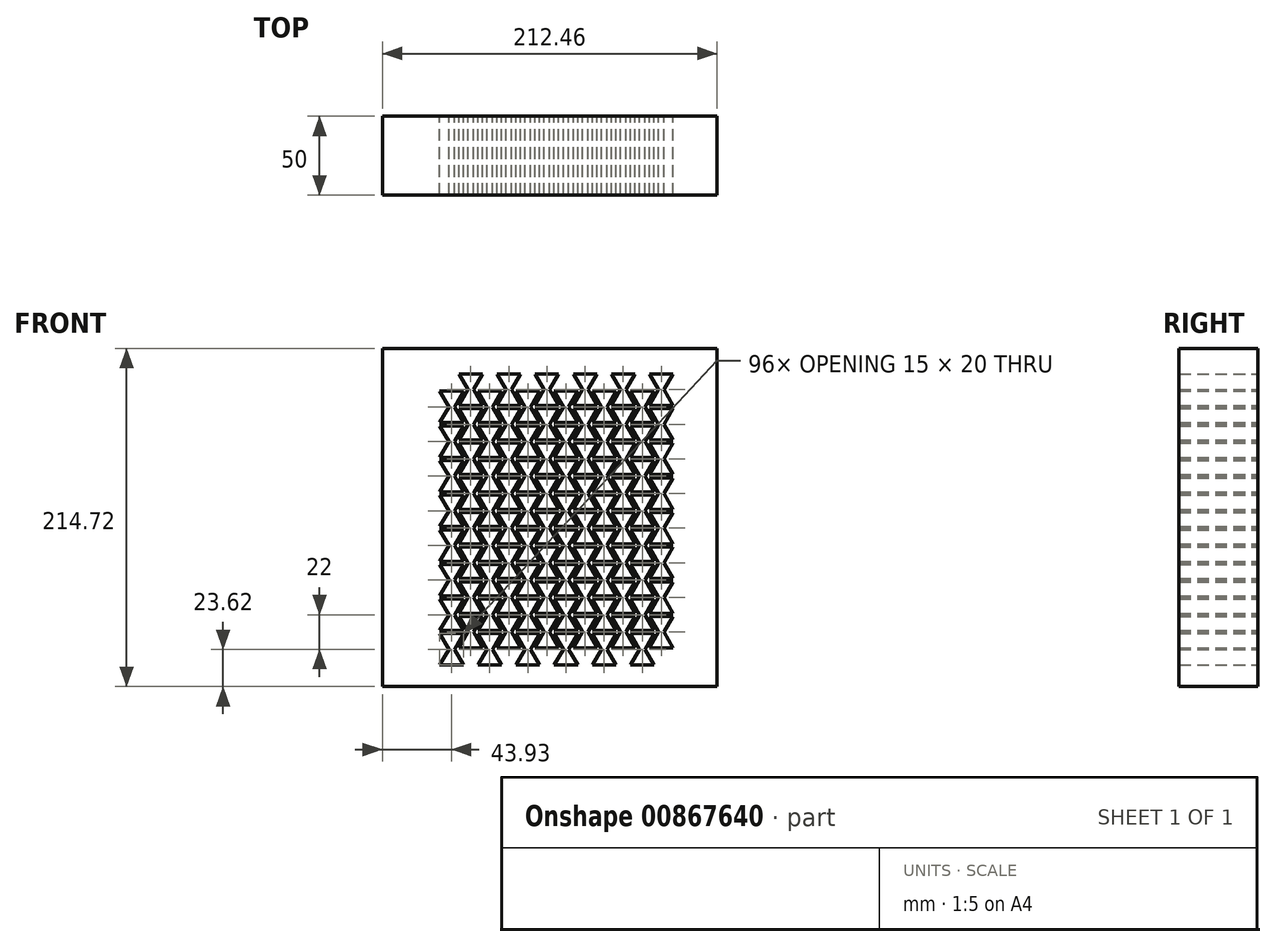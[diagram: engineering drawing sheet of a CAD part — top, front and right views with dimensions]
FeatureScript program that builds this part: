
annotation { "Feature Type Name" : "Feature", "Feature Type Description" : "" }
export const myFeature = defineFeature(function(context is Context, id is Id, definition is map)
    precondition{}
    {
        {
            var Q0;
            Q0=qCreatedBy(makeId("Front.planeOp"),FACE);
            var sketch = newSketch(context, id + "F0", { "sketchPlane" : qUnion([Q0])});
            skLineSegment(sketch, "E0", {"start": v(0, 0) * mm, "end": v(15, 0) * mm});
            skLineSegment(sketch, "E1", {"start": v(0, 20) * mm, "end": v(15, 20) * mm});
            skLineSegment(sketch, "E2", {"start": v(0, 20) * mm, "end": v(5.77, 10) * mm});
            skLineSegment(sketch, "E3", {"start": v(5.77, 10) * mm, "end": v(0, 0) * mm});
            skLineSegment(sketch, "E4", {"start": v(15, 20) * mm, "end": v(9.23, 10) * mm});
            skLineSegment(sketch, "E5", {"start": v(9.23, 10) * mm, "end": v(15, 0) * mm});
            skPoint(sketch, "E6", {"position": v(7.5, 21) * mm});
            skPoint(sketch, "E6.positionSnap0", {"position": v(7.5, 20) * mm});
            skPoint(sketch, "E7", {"position": v(7.5, -1) * mm});
            skPoint(sketch, "E7.positionSnap0", {"position": v(7.5, 0) * mm});
            skPoint(sketch, "E8", {"position": v(1.44, 4.5) * mm});
            skPoint(sketch, "E9", {"position": v(13.56, 4.5) * mm});
            skPoint(sketch, "E10", {"position": v(13.66, 15.67) * mm});
            skPoint(sketch, "E11", {"position": v(0.66, 16.85) * mm});
            skLineSegment(sketch, "E12", {"start": v(10.38, 10) * mm, "end": v(10.04, 10.6) * mm});
            skPoint(sketch, "E13", {"position": v(-1.73, 21) * mm});
            skPoint(sketch, "E14", {"position": v(16.73, 21) * mm});
            skPoint(sketch, "E15", {"position": v(4.62, 10) * mm});
            skPoint(sketch, "E16", {"position": v(10.38, 10) * mm});
            skPoint(sketch, "E17", {"position": v(-1.73, -1) * mm});
            skPoint(sketch, "E18", {"position": v(16.73, -1) * mm});
            skLineSegment(sketch, "E19", {"start": v(0, 22) * mm, "end": v(15, 22) * mm});
            skLineSegment(sketch, "E20", {"start": v(0, 42) * mm, "end": v(15, 42) * mm});
            skLineSegment(sketch, "E21", {"start": v(0, 42) * mm, "end": v(5.77, 32) * mm});
            skLineSegment(sketch, "E22", {"start": v(5.77, 32) * mm, "end": v(0, 22) * mm});
            skLineSegment(sketch, "E23", {"start": v(15, 42) * mm, "end": v(9.23, 32) * mm});
            skLineSegment(sketch, "E24", {"start": v(9.23, 32) * mm, "end": v(15, 22) * mm});
            skPoint(sketch, "E25", {"position": v(7.5, 43) * mm});
            skPoint(sketch, "E25.positionSnap0", {"position": v(7.5, 42) * mm});
            skPoint(sketch, "E26.positionSnap0", {"position": v(7.5, 22) * mm});
            skPoint(sketch, "E27", {"position": v(1.44, 26.5) * mm});
            skPoint(sketch, "E28", {"position": v(13.56, 26.5) * mm});
            skPoint(sketch, "E29", {"position": v(13.66, 37.67) * mm});
            skPoint(sketch, "E30", {"position": v(0.66, 38.85) * mm});
            skLineSegment(sketch, "E31", {"start": v(10.38, 32) * mm, "end": v(10.04, 32.6) * mm});
            skPoint(sketch, "E32", {"position": v(-1.73, 43) * mm});
            skPoint(sketch, "E33", {"position": v(16.73, 43) * mm});
            skPoint(sketch, "E34", {"position": v(4.62, 32) * mm});
            skPoint(sketch, "E35", {"position": v(10.38, 32) * mm});
            skLineSegment(sketch, "E36", {"start": v(0, 44) * mm, "end": v(15, 44) * mm});
            skLineSegment(sketch, "E37", {"start": v(0, 64) * mm, "end": v(15, 64) * mm});
            skLineSegment(sketch, "E38", {"start": v(0, 64) * mm, "end": v(5.77, 54) * mm});
            skLineSegment(sketch, "E39", {"start": v(5.77, 54) * mm, "end": v(0, 44) * mm});
            skLineSegment(sketch, "E40", {"start": v(15, 64) * mm, "end": v(9.23, 54) * mm});
            skLineSegment(sketch, "E41", {"start": v(9.23, 54) * mm, "end": v(15, 44) * mm});
            skPoint(sketch, "E42", {"position": v(7.5, 65) * mm});
            skPoint(sketch, "E42.positionSnap0", {"position": v(7.5, 64) * mm});
            skPoint(sketch, "E43.positionSnap0", {"position": v(7.5, 44) * mm});
            skPoint(sketch, "E44", {"position": v(1.44, 48.5) * mm});
            skPoint(sketch, "E45", {"position": v(13.56, 48.5) * mm});
            skPoint(sketch, "E46", {"position": v(13.66, 59.67) * mm});
            skPoint(sketch, "E47", {"position": v(0.66, 60.85) * mm});
            skLineSegment(sketch, "E48", {"start": v(10.38, 54) * mm, "end": v(10.04, 54.6) * mm});
            skPoint(sketch, "E49", {"position": v(-1.73, 65) * mm});
            skPoint(sketch, "E50", {"position": v(16.73, 65) * mm});
            skPoint(sketch, "E51", {"position": v(4.62, 54) * mm});
            skPoint(sketch, "E52", {"position": v(10.38, 54) * mm});
            skLineSegment(sketch, "E53", {"start": v(0, 66) * mm, "end": v(15, 66) * mm});
            skLineSegment(sketch, "E54", {"start": v(0, 86) * mm, "end": v(15, 86) * mm});
            skLineSegment(sketch, "E55", {"start": v(0, 86) * mm, "end": v(5.77, 76) * mm});
            skLineSegment(sketch, "E56", {"start": v(5.77, 76) * mm, "end": v(0, 66) * mm});
            skLineSegment(sketch, "E57", {"start": v(15, 86) * mm, "end": v(9.23, 76) * mm});
            skLineSegment(sketch, "E58", {"start": v(9.23, 76) * mm, "end": v(15, 66) * mm});
            skPoint(sketch, "E59", {"position": v(7.5, 87) * mm});
            skPoint(sketch, "E59.positionSnap0", {"position": v(7.5, 86) * mm});
            skPoint(sketch, "E60.positionSnap0", {"position": v(7.5, 66) * mm});
            skPoint(sketch, "E61", {"position": v(1.44, 70.5) * mm});
            skPoint(sketch, "E62", {"position": v(13.56, 70.5) * mm});
            skPoint(sketch, "E63", {"position": v(13.66, 81.67) * mm});
            skPoint(sketch, "E64", {"position": v(0.66, 82.85) * mm});
            skLineSegment(sketch, "E65", {"start": v(10.38, 76) * mm, "end": v(10.04, 76.6) * mm});
            skPoint(sketch, "E66", {"position": v(-1.73, 87) * mm});
            skPoint(sketch, "E67", {"position": v(16.73, 87) * mm});
            skPoint(sketch, "E68", {"position": v(4.62, 76) * mm});
            skPoint(sketch, "E69", {"position": v(10.38, 76) * mm});
            skLineSegment(sketch, "E70", {"start": v(0, 88) * mm, "end": v(15, 88) * mm});
            skLineSegment(sketch, "E71", {"start": v(0, 108) * mm, "end": v(15, 108) * mm});
            skLineSegment(sketch, "E72", {"start": v(0, 108) * mm, "end": v(5.77, 98) * mm});
            skLineSegment(sketch, "E73", {"start": v(5.77, 98) * mm, "end": v(0, 88) * mm});
            skLineSegment(sketch, "E74", {"start": v(15, 108) * mm, "end": v(9.23, 98) * mm});
            skLineSegment(sketch, "E75", {"start": v(9.23, 98) * mm, "end": v(15, 88) * mm});
            skPoint(sketch, "E76", {"position": v(7.5, 109) * mm});
            skPoint(sketch, "E76.positionSnap0", {"position": v(7.5, 108) * mm});
            skPoint(sketch, "E77.positionSnap0", {"position": v(7.5, 88) * mm});
            skPoint(sketch, "E78", {"position": v(1.44, 92.5) * mm});
            skPoint(sketch, "E79", {"position": v(13.56, 92.5) * mm});
            skPoint(sketch, "E80", {"position": v(13.66, 103.67) * mm});
            skPoint(sketch, "E81", {"position": v(0.66, 104.85) * mm});
            skLineSegment(sketch, "E82", {"start": v(10.38, 98) * mm, "end": v(10.04, 98.6) * mm});
            skPoint(sketch, "E83", {"position": v(-1.73, 109) * mm});
            skPoint(sketch, "E84", {"position": v(16.73, 109) * mm});
            skPoint(sketch, "E85", {"position": v(4.62, 98) * mm});
            skPoint(sketch, "E86", {"position": v(10.38, 98) * mm});
            skLineSegment(sketch, "E87", {"start": v(0, 110) * mm, "end": v(15, 110) * mm});
            skLineSegment(sketch, "E88", {"start": v(0, 130) * mm, "end": v(15, 130) * mm});
            skLineSegment(sketch, "E89", {"start": v(0, 130) * mm, "end": v(5.77, 120) * mm});
            skLineSegment(sketch, "E90", {"start": v(5.77, 120) * mm, "end": v(0, 110) * mm});
            skLineSegment(sketch, "E91", {"start": v(15, 130) * mm, "end": v(9.23, 120) * mm});
            skLineSegment(sketch, "E92", {"start": v(9.23, 120) * mm, "end": v(15, 110) * mm});
            skPoint(sketch, "E93", {"position": v(7.5, 131) * mm});
            skPoint(sketch, "E93.positionSnap0", {"position": v(7.5, 130) * mm});
            skPoint(sketch, "E94.positionSnap0", {"position": v(7.5, 110) * mm});
            skPoint(sketch, "E95", {"position": v(1.44, 114.5) * mm});
            skPoint(sketch, "E96", {"position": v(13.56, 114.5) * mm});
            skPoint(sketch, "E97", {"position": v(13.66, 125.67) * mm});
            skPoint(sketch, "E98", {"position": v(0.66, 126.85) * mm});
            skLineSegment(sketch, "E99", {"start": v(10.38, 120) * mm, "end": v(10.04, 120.6) * mm});
            skPoint(sketch, "E100", {"position": v(-1.73, 131) * mm});
            skPoint(sketch, "E101", {"position": v(16.73, 131) * mm});
            skPoint(sketch, "E102", {"position": v(4.62, 120) * mm});
            skPoint(sketch, "E103", {"position": v(10.38, 120) * mm});
            skLineSegment(sketch, "E104", {"start": v(0, 132) * mm, "end": v(15, 132) * mm});
            skLineSegment(sketch, "E105", {"start": v(0, 152) * mm, "end": v(15, 152) * mm});
            skLineSegment(sketch, "E106", {"start": v(0, 152) * mm, "end": v(5.77, 142) * mm});
            skLineSegment(sketch, "E107", {"start": v(5.77, 142) * mm, "end": v(0, 132) * mm});
            skLineSegment(sketch, "E108", {"start": v(15, 152) * mm, "end": v(9.23, 142) * mm});
            skLineSegment(sketch, "E109", {"start": v(9.23, 142) * mm, "end": v(15, 132) * mm});
            skPoint(sketch, "E110", {"position": v(7.5, 153) * mm});
            skPoint(sketch, "E110.positionSnap0", {"position": v(7.5, 152) * mm});
            skPoint(sketch, "E111.positionSnap0", {"position": v(7.5, 132) * mm});
            skPoint(sketch, "E112", {"position": v(1.44, 136.5) * mm});
            skPoint(sketch, "E113", {"position": v(13.56, 136.5) * mm});
            skPoint(sketch, "E114", {"position": v(13.66, 147.67) * mm});
            skPoint(sketch, "E115", {"position": v(0.66, 148.85) * mm});
            skLineSegment(sketch, "E116", {"start": v(10.38, 142) * mm, "end": v(10.04, 142.6) * mm});
            skPoint(sketch, "E117", {"position": v(-1.73, 153) * mm});
            skPoint(sketch, "E118", {"position": v(16.73, 153) * mm});
            skPoint(sketch, "E119", {"position": v(4.62, 142) * mm});
            skPoint(sketch, "E120", {"position": v(10.38, 142) * mm});
            skLineSegment(sketch, "E121", {"start": v(0, 154) * mm, "end": v(15, 154) * mm});
            skLineSegment(sketch, "E122", {"start": v(0, 174) * mm, "end": v(15, 174) * mm});
            skLineSegment(sketch, "E123", {"start": v(0, 174) * mm, "end": v(5.77, 164) * mm});
            skLineSegment(sketch, "E124", {"start": v(5.77, 164) * mm, "end": v(0, 154) * mm});
            skLineSegment(sketch, "E125", {"start": v(15, 174) * mm, "end": v(9.23, 164) * mm});
            skLineSegment(sketch, "E126", {"start": v(9.23, 164) * mm, "end": v(15, 154) * mm});
            skPoint(sketch, "E127", {"position": v(7.5, 175) * mm});
            skPoint(sketch, "E127.positionSnap0", {"position": v(7.5, 174) * mm});
            skPoint(sketch, "E128.positionSnap0", {"position": v(7.5, 154) * mm});
            skPoint(sketch, "E129", {"position": v(1.44, 158.5) * mm});
            skPoint(sketch, "E130", {"position": v(13.56, 158.5) * mm});
            skPoint(sketch, "E131", {"position": v(13.66, 169.67) * mm});
            skPoint(sketch, "E132", {"position": v(0.66, 170.85) * mm});
            skLineSegment(sketch, "E133", {"start": v(10.38, 164) * mm, "end": v(10.04, 164.6) * mm});
            skPoint(sketch, "E134", {"position": v(-1.73, 175) * mm});
            skPoint(sketch, "E135", {"position": v(16.73, 175) * mm});
            skPoint(sketch, "E136", {"position": v(4.62, 164) * mm});
            skPoint(sketch, "E137", {"position": v(10.38, 164) * mm});
            skLineSegment(sketch, "E138", {"start": v(12.11, 11) * mm, "end": v(27.11, 11) * mm});
            skLineSegment(sketch, "E139", {"start": v(12.11, 31) * mm, "end": v(27.11, 31) * mm});
            skLineSegment(sketch, "E140", {"start": v(12.11, 31) * mm, "end": v(17.89, 21) * mm});
            skLineSegment(sketch, "E141", {"start": v(17.89, 21) * mm, "end": v(12.11, 11) * mm});
            skLineSegment(sketch, "E142", {"start": v(27.11, 31) * mm, "end": v(21.34, 21) * mm});
            skLineSegment(sketch, "E143", {"start": v(21.34, 21) * mm, "end": v(27.11, 11) * mm});
            skPoint(sketch, "E144", {"position": v(19.61, 32) * mm});
            skPoint(sketch, "E144.positionSnap0", {"position": v(19.61, 31) * mm});
            skPoint(sketch, "E145", {"position": v(19.61, 10) * mm});
            skPoint(sketch, "E145.positionSnap0", {"position": v(19.61, 11) * mm});
            skPoint(sketch, "E146", {"position": v(13.55, 15.5) * mm});
            skPoint(sketch, "E147", {"position": v(25.67, 15.5) * mm});
            skPoint(sketch, "E148", {"position": v(25.77, 26.67) * mm});
            skPoint(sketch, "E149", {"position": v(12.78, 27.85) * mm});
            skLineSegment(sketch, "E150", {"start": v(22.5, 21) * mm, "end": v(22.15, 21.6) * mm});
            skPoint(sketch, "E151", {"position": v(28.85, 32) * mm});
            skPoint(sketch, "E152", {"position": v(22.5, 21) * mm});
            skPoint(sketch, "E153", {"position": v(28.85, 10) * mm});
            skLineSegment(sketch, "E154", {"start": v(12.11, 33) * mm, "end": v(27.11, 33) * mm});
            skLineSegment(sketch, "E155", {"start": v(12.11, 53) * mm, "end": v(27.11, 53) * mm});
            skLineSegment(sketch, "E156", {"start": v(12.11, 53) * mm, "end": v(17.89, 43) * mm});
            skLineSegment(sketch, "E157", {"start": v(17.89, 43) * mm, "end": v(12.11, 33) * mm});
            skLineSegment(sketch, "E158", {"start": v(27.11, 53) * mm, "end": v(21.34, 43) * mm});
            skLineSegment(sketch, "E159", {"start": v(21.34, 43) * mm, "end": v(27.11, 33) * mm});
            skPoint(sketch, "E160", {"position": v(19.61, 54) * mm});
            skPoint(sketch, "E160.positionSnap0", {"position": v(19.61, 53) * mm});
            skPoint(sketch, "E161.positionSnap0", {"position": v(19.61, 33) * mm});
            skPoint(sketch, "E162", {"position": v(13.55, 37.5) * mm});
            skPoint(sketch, "E163", {"position": v(25.67, 37.5) * mm});
            skPoint(sketch, "E164", {"position": v(25.77, 48.67) * mm});
            skPoint(sketch, "E165", {"position": v(12.78, 49.85) * mm});
            skLineSegment(sketch, "E166", {"start": v(22.5, 43) * mm, "end": v(22.15, 43.6) * mm});
            skPoint(sketch, "E167", {"position": v(28.85, 54) * mm});
            skPoint(sketch, "E168", {"position": v(22.5, 43) * mm});
            skLineSegment(sketch, "E169", {"start": v(12.11, 55) * mm, "end": v(27.11, 55) * mm});
            skLineSegment(sketch, "E170", {"start": v(12.11, 75) * mm, "end": v(27.11, 75) * mm});
            skLineSegment(sketch, "E171", {"start": v(12.11, 75) * mm, "end": v(17.89, 65) * mm});
            skLineSegment(sketch, "E172", {"start": v(17.89, 65) * mm, "end": v(12.11, 55) * mm});
            skLineSegment(sketch, "E173", {"start": v(27.11, 75) * mm, "end": v(21.34, 65) * mm});
            skLineSegment(sketch, "E174", {"start": v(21.34, 65) * mm, "end": v(27.11, 55) * mm});
            skPoint(sketch, "E175", {"position": v(19.61, 76) * mm});
            skPoint(sketch, "E175.positionSnap0", {"position": v(19.61, 75) * mm});
            skPoint(sketch, "E176.positionSnap0", {"position": v(19.61, 55) * mm});
            skPoint(sketch, "E177", {"position": v(13.55, 59.5) * mm});
            skPoint(sketch, "E178", {"position": v(25.67, 59.5) * mm});
            skPoint(sketch, "E179", {"position": v(25.77, 70.67) * mm});
            skPoint(sketch, "E180", {"position": v(12.78, 71.85) * mm});
            skLineSegment(sketch, "E181", {"start": v(22.5, 65) * mm, "end": v(22.15, 65.6) * mm});
            skPoint(sketch, "E182", {"position": v(28.85, 76) * mm});
            skPoint(sketch, "E183", {"position": v(22.5, 65) * mm});
            skLineSegment(sketch, "E184", {"start": v(12.11, 77) * mm, "end": v(27.11, 77) * mm});
            skLineSegment(sketch, "E185", {"start": v(12.11, 97) * mm, "end": v(27.11, 97) * mm});
            skLineSegment(sketch, "E186", {"start": v(12.11, 97) * mm, "end": v(17.89, 87) * mm});
            skLineSegment(sketch, "E187", {"start": v(17.89, 87) * mm, "end": v(12.11, 77) * mm});
            skLineSegment(sketch, "E188", {"start": v(27.11, 97) * mm, "end": v(21.34, 87) * mm});
            skLineSegment(sketch, "E189", {"start": v(21.34, 87) * mm, "end": v(27.11, 77) * mm});
            skPoint(sketch, "E190", {"position": v(19.61, 98) * mm});
            skPoint(sketch, "E190.positionSnap0", {"position": v(19.61, 97) * mm});
            skPoint(sketch, "E191.positionSnap0", {"position": v(19.61, 77) * mm});
            skPoint(sketch, "E192", {"position": v(13.55, 81.5) * mm});
            skPoint(sketch, "E193", {"position": v(25.67, 81.5) * mm});
            skPoint(sketch, "E194", {"position": v(25.77, 92.67) * mm});
            skPoint(sketch, "E195", {"position": v(12.78, 93.85) * mm});
            skLineSegment(sketch, "E196", {"start": v(22.5, 87) * mm, "end": v(22.15, 87.6) * mm});
            skPoint(sketch, "E197", {"position": v(28.85, 98) * mm});
            skPoint(sketch, "E198", {"position": v(22.5, 87) * mm});
            skLineSegment(sketch, "E199", {"start": v(12.11, 99) * mm, "end": v(27.11, 99) * mm});
            skLineSegment(sketch, "E200", {"start": v(12.11, 119) * mm, "end": v(27.11, 119) * mm});
            skLineSegment(sketch, "E201", {"start": v(12.11, 119) * mm, "end": v(17.89, 109) * mm});
            skLineSegment(sketch, "E202", {"start": v(17.89, 109) * mm, "end": v(12.11, 99) * mm});
            skLineSegment(sketch, "E203", {"start": v(27.11, 119) * mm, "end": v(21.34, 109) * mm});
            skLineSegment(sketch, "E204", {"start": v(21.34, 109) * mm, "end": v(27.11, 99) * mm});
            skPoint(sketch, "E205", {"position": v(19.61, 120) * mm});
            skPoint(sketch, "E205.positionSnap0", {"position": v(19.61, 119) * mm});
            skPoint(sketch, "E206.positionSnap0", {"position": v(19.61, 99) * mm});
            skPoint(sketch, "E207", {"position": v(13.55, 103.5) * mm});
            skPoint(sketch, "E208", {"position": v(25.67, 103.5) * mm});
            skPoint(sketch, "E209", {"position": v(25.77, 114.67) * mm});
            skPoint(sketch, "E210", {"position": v(12.78, 115.85) * mm});
            skLineSegment(sketch, "E211", {"start": v(22.5, 109) * mm, "end": v(22.15, 109.6) * mm});
            skPoint(sketch, "E212", {"position": v(28.85, 120) * mm});
            skPoint(sketch, "E213", {"position": v(22.5, 109) * mm});
            skLineSegment(sketch, "E214", {"start": v(12.11, 121) * mm, "end": v(27.11, 121) * mm});
            skLineSegment(sketch, "E215", {"start": v(12.11, 141) * mm, "end": v(27.11, 141) * mm});
            skLineSegment(sketch, "E216", {"start": v(12.11, 141) * mm, "end": v(17.89, 131) * mm});
            skLineSegment(sketch, "E217", {"start": v(17.89, 131) * mm, "end": v(12.11, 121) * mm});
            skLineSegment(sketch, "E218", {"start": v(27.11, 141) * mm, "end": v(21.34, 131) * mm});
            skLineSegment(sketch, "E219", {"start": v(21.34, 131) * mm, "end": v(27.11, 121) * mm});
            skPoint(sketch, "E220", {"position": v(19.61, 142) * mm});
            skPoint(sketch, "E220.positionSnap0", {"position": v(19.61, 141) * mm});
            skPoint(sketch, "E221.positionSnap0", {"position": v(19.61, 121) * mm});
            skPoint(sketch, "E222", {"position": v(13.55, 125.5) * mm});
            skPoint(sketch, "E223", {"position": v(25.67, 125.5) * mm});
            skPoint(sketch, "E224", {"position": v(25.77, 136.67) * mm});
            skPoint(sketch, "E225", {"position": v(12.78, 137.85) * mm});
            skLineSegment(sketch, "E226", {"start": v(22.5, 131) * mm, "end": v(22.15, 131.6) * mm});
            skPoint(sketch, "E227", {"position": v(28.85, 142) * mm});
            skPoint(sketch, "E228", {"position": v(22.5, 131) * mm});
            skLineSegment(sketch, "E229", {"start": v(12.11, 143) * mm, "end": v(27.11, 143) * mm});
            skLineSegment(sketch, "E230", {"start": v(12.11, 163) * mm, "end": v(27.11, 163) * mm});
            skLineSegment(sketch, "E231", {"start": v(12.11, 163) * mm, "end": v(17.89, 153) * mm});
            skLineSegment(sketch, "E232", {"start": v(17.89, 153) * mm, "end": v(12.11, 143) * mm});
            skLineSegment(sketch, "E233", {"start": v(27.11, 163) * mm, "end": v(21.34, 153) * mm});
            skLineSegment(sketch, "E234", {"start": v(21.34, 153) * mm, "end": v(27.11, 143) * mm});
            skPoint(sketch, "E235", {"position": v(19.61, 164) * mm});
            skPoint(sketch, "E235.positionSnap0", {"position": v(19.61, 163) * mm});
            skPoint(sketch, "E236.positionSnap0", {"position": v(19.61, 143) * mm});
            skPoint(sketch, "E237", {"position": v(13.55, 147.5) * mm});
            skPoint(sketch, "E238", {"position": v(25.67, 147.5) * mm});
            skPoint(sketch, "E239", {"position": v(25.77, 158.67) * mm});
            skPoint(sketch, "E240", {"position": v(12.78, 159.85) * mm});
            skLineSegment(sketch, "E241", {"start": v(22.5, 153) * mm, "end": v(22.15, 153.6) * mm});
            skPoint(sketch, "E242", {"position": v(28.85, 164) * mm});
            skPoint(sketch, "E243", {"position": v(22.5, 153) * mm});
            skLineSegment(sketch, "E244", {"start": v(12.11, 165) * mm, "end": v(27.11, 165) * mm});
            skLineSegment(sketch, "E245", {"start": v(12.11, 185) * mm, "end": v(27.11, 185) * mm});
            skLineSegment(sketch, "E246", {"start": v(12.11, 185) * mm, "end": v(17.89, 175) * mm});
            skLineSegment(sketch, "E247", {"start": v(17.89, 175) * mm, "end": v(12.11, 165) * mm});
            skLineSegment(sketch, "E248", {"start": v(27.11, 185) * mm, "end": v(21.34, 175) * mm});
            skLineSegment(sketch, "E249", {"start": v(21.34, 175) * mm, "end": v(27.11, 165) * mm});
            skPoint(sketch, "E250", {"position": v(19.61, 186) * mm});
            skPoint(sketch, "E250.positionSnap0", {"position": v(19.61, 185) * mm});
            skPoint(sketch, "E251.positionSnap0", {"position": v(19.61, 165) * mm});
            skPoint(sketch, "E252", {"position": v(13.55, 169.5) * mm});
            skPoint(sketch, "E253", {"position": v(25.67, 169.5) * mm});
            skPoint(sketch, "E254", {"position": v(25.77, 180.67) * mm});
            skPoint(sketch, "E255", {"position": v(12.78, 181.85) * mm});
            skLineSegment(sketch, "E256", {"start": v(22.5, 175) * mm, "end": v(22.15, 175.6) * mm});
            skPoint(sketch, "E257", {"position": v(10.38, 186) * mm});
            skPoint(sketch, "E258", {"position": v(28.85, 186) * mm});
            skPoint(sketch, "E259", {"position": v(22.5, 175) * mm});
            skLineSegment(sketch, "E260", {"start": v(24.23, 0) * mm, "end": v(39.23, 0) * mm});
            skLineSegment(sketch, "E261", {"start": v(24.23, 20) * mm, "end": v(39.23, 20) * mm});
            skLineSegment(sketch, "E262", {"start": v(24.23, 20) * mm, "end": v(30, 10) * mm});
            skLineSegment(sketch, "E263", {"start": v(30, 10) * mm, "end": v(24.23, 0) * mm});
            skLineSegment(sketch, "E264", {"start": v(39.23, 20) * mm, "end": v(33.45, 10) * mm});
            skLineSegment(sketch, "E265", {"start": v(33.45, 10) * mm, "end": v(39.23, 0) * mm});
            skPoint(sketch, "E266", {"position": v(31.73, 21) * mm});
            skPoint(sketch, "E266.positionSnap0", {"position": v(31.73, 20) * mm});
            skPoint(sketch, "E267", {"position": v(31.73, -1) * mm});
            skPoint(sketch, "E267.positionSnap0", {"position": v(31.73, 0) * mm});
            skPoint(sketch, "E268", {"position": v(25.67, 4.5) * mm});
            skPoint(sketch, "E269", {"position": v(37.79, 4.5) * mm});
            skPoint(sketch, "E270", {"position": v(37.88, 15.67) * mm});
            skPoint(sketch, "E271", {"position": v(24.9, 16.85) * mm});
            skLineSegment(sketch, "E272", {"start": v(34.6, 10) * mm, "end": v(34.26, 10.6) * mm});
            skPoint(sketch, "E273", {"position": v(40.96, 21) * mm});
            skPoint(sketch, "E274", {"position": v(34.6, 10) * mm});
            skPoint(sketch, "E275", {"position": v(22.5, -1) * mm});
            skPoint(sketch, "E276", {"position": v(40.96, -1) * mm});
            skLineSegment(sketch, "E277", {"start": v(24.23, 22) * mm, "end": v(39.23, 22) * mm});
            skLineSegment(sketch, "E278", {"start": v(24.23, 42) * mm, "end": v(39.23, 42) * mm});
            skLineSegment(sketch, "E279", {"start": v(24.23, 42) * mm, "end": v(30, 32) * mm});
            skLineSegment(sketch, "E280", {"start": v(30, 32) * mm, "end": v(24.23, 22) * mm});
            skLineSegment(sketch, "E281", {"start": v(39.23, 42) * mm, "end": v(33.45, 32) * mm});
            skLineSegment(sketch, "E282", {"start": v(33.45, 32) * mm, "end": v(39.23, 22) * mm});
            skPoint(sketch, "E283", {"position": v(31.73, 43) * mm});
            skPoint(sketch, "E283.positionSnap0", {"position": v(31.73, 42) * mm});
            skPoint(sketch, "E284.positionSnap0", {"position": v(31.73, 22) * mm});
            skPoint(sketch, "E285", {"position": v(25.67, 26.5) * mm});
            skPoint(sketch, "E286", {"position": v(37.79, 26.5) * mm});
            skPoint(sketch, "E287", {"position": v(37.88, 37.67) * mm});
            skPoint(sketch, "E288", {"position": v(24.9, 38.85) * mm});
            skLineSegment(sketch, "E289", {"start": v(34.6, 32) * mm, "end": v(34.26, 32.6) * mm});
            skPoint(sketch, "E290", {"position": v(40.96, 43) * mm});
            skPoint(sketch, "E291", {"position": v(34.6, 32) * mm});
            skLineSegment(sketch, "E292", {"start": v(24.23, 44) * mm, "end": v(39.23, 44) * mm});
            skLineSegment(sketch, "E293", {"start": v(24.23, 64) * mm, "end": v(39.23, 64) * mm});
            skLineSegment(sketch, "E294", {"start": v(24.23, 64) * mm, "end": v(30, 54) * mm});
            skLineSegment(sketch, "E295", {"start": v(30, 54) * mm, "end": v(24.23, 44) * mm});
            skLineSegment(sketch, "E296", {"start": v(39.23, 64) * mm, "end": v(33.45, 54) * mm});
            skLineSegment(sketch, "E297", {"start": v(33.45, 54) * mm, "end": v(39.23, 44) * mm});
            skPoint(sketch, "E298", {"position": v(31.73, 65) * mm});
            skPoint(sketch, "E298.positionSnap0", {"position": v(31.73, 64) * mm});
            skPoint(sketch, "E299.positionSnap0", {"position": v(31.73, 44) * mm});
            skPoint(sketch, "E300", {"position": v(25.67, 48.5) * mm});
            skPoint(sketch, "E301", {"position": v(37.79, 48.5) * mm});
            skPoint(sketch, "E302", {"position": v(37.88, 59.67) * mm});
            skPoint(sketch, "E303", {"position": v(24.9, 60.85) * mm});
            skLineSegment(sketch, "E304", {"start": v(34.6, 54) * mm, "end": v(34.26, 54.6) * mm});
            skPoint(sketch, "E305", {"position": v(40.96, 65) * mm});
            skPoint(sketch, "E306", {"position": v(34.6, 54) * mm});
            skLineSegment(sketch, "E307", {"start": v(24.23, 66) * mm, "end": v(39.23, 66) * mm});
            skLineSegment(sketch, "E308", {"start": v(24.23, 86) * mm, "end": v(39.23, 86) * mm});
            skLineSegment(sketch, "E309", {"start": v(24.23, 86) * mm, "end": v(30, 76) * mm});
            skLineSegment(sketch, "E310", {"start": v(30, 76) * mm, "end": v(24.23, 66) * mm});
            skLineSegment(sketch, "E311", {"start": v(39.23, 86) * mm, "end": v(33.45, 76) * mm});
            skLineSegment(sketch, "E312", {"start": v(33.45, 76) * mm, "end": v(39.23, 66) * mm});
            skPoint(sketch, "E313", {"position": v(31.73, 87) * mm});
            skPoint(sketch, "E313.positionSnap0", {"position": v(31.73, 86) * mm});
            skPoint(sketch, "E314.positionSnap0", {"position": v(31.73, 66) * mm});
            skPoint(sketch, "E315", {"position": v(25.67, 70.5) * mm});
            skPoint(sketch, "E316", {"position": v(37.79, 70.5) * mm});
            skPoint(sketch, "E317", {"position": v(37.88, 81.67) * mm});
            skPoint(sketch, "E318", {"position": v(24.9, 82.85) * mm});
            skLineSegment(sketch, "E319", {"start": v(34.6, 76) * mm, "end": v(34.26, 76.6) * mm});
            skPoint(sketch, "E320", {"position": v(40.96, 87) * mm});
            skPoint(sketch, "E321", {"position": v(34.6, 76) * mm});
            skLineSegment(sketch, "E322", {"start": v(24.23, 88) * mm, "end": v(39.23, 88) * mm});
            skLineSegment(sketch, "E323", {"start": v(24.23, 108) * mm, "end": v(39.23, 108) * mm});
            skLineSegment(sketch, "E324", {"start": v(24.23, 108) * mm, "end": v(30, 98) * mm});
            skLineSegment(sketch, "E325", {"start": v(30, 98) * mm, "end": v(24.23, 88) * mm});
            skLineSegment(sketch, "E326", {"start": v(39.23, 108) * mm, "end": v(33.45, 98) * mm});
            skLineSegment(sketch, "E327", {"start": v(33.45, 98) * mm, "end": v(39.23, 88) * mm});
            skPoint(sketch, "E328", {"position": v(31.73, 109) * mm});
            skPoint(sketch, "E328.positionSnap0", {"position": v(31.73, 108) * mm});
            skPoint(sketch, "E329.positionSnap0", {"position": v(31.73, 88) * mm});
            skPoint(sketch, "E330", {"position": v(25.67, 92.5) * mm});
            skPoint(sketch, "E331", {"position": v(37.79, 92.5) * mm});
            skPoint(sketch, "E332", {"position": v(37.88, 103.67) * mm});
            skPoint(sketch, "E333", {"position": v(24.9, 104.85) * mm});
            skLineSegment(sketch, "E334", {"start": v(34.6, 98) * mm, "end": v(34.26, 98.6) * mm});
            skPoint(sketch, "E335", {"position": v(40.96, 109) * mm});
            skPoint(sketch, "E336", {"position": v(34.6, 98) * mm});
            skLineSegment(sketch, "E337", {"start": v(24.23, 110) * mm, "end": v(39.23, 110) * mm});
            skLineSegment(sketch, "E338", {"start": v(24.23, 130) * mm, "end": v(39.23, 130) * mm});
            skLineSegment(sketch, "E339", {"start": v(24.23, 130) * mm, "end": v(30, 120) * mm});
            skLineSegment(sketch, "E340", {"start": v(30, 120) * mm, "end": v(24.23, 110) * mm});
            skLineSegment(sketch, "E341", {"start": v(39.23, 130) * mm, "end": v(33.45, 120) * mm});
            skLineSegment(sketch, "E342", {"start": v(33.45, 120) * mm, "end": v(39.23, 110) * mm});
            skPoint(sketch, "E343", {"position": v(31.73, 131) * mm});
            skPoint(sketch, "E343.positionSnap0", {"position": v(31.73, 130) * mm});
            skPoint(sketch, "E344.positionSnap0", {"position": v(31.73, 110) * mm});
            skPoint(sketch, "E345", {"position": v(25.67, 114.5) * mm});
            skPoint(sketch, "E346", {"position": v(37.79, 114.5) * mm});
            skPoint(sketch, "E347", {"position": v(37.88, 125.67) * mm});
            skPoint(sketch, "E348", {"position": v(24.9, 126.85) * mm});
            skLineSegment(sketch, "E349", {"start": v(34.6, 120) * mm, "end": v(34.26, 120.6) * mm});
            skPoint(sketch, "E350", {"position": v(40.96, 131) * mm});
            skPoint(sketch, "E351", {"position": v(34.6, 120) * mm});
            skLineSegment(sketch, "E352", {"start": v(24.23, 132) * mm, "end": v(39.23, 132) * mm});
            skLineSegment(sketch, "E353", {"start": v(24.23, 152) * mm, "end": v(39.23, 152) * mm});
            skLineSegment(sketch, "E354", {"start": v(24.23, 152) * mm, "end": v(30, 142) * mm});
            skLineSegment(sketch, "E355", {"start": v(30, 142) * mm, "end": v(24.23, 132) * mm});
            skLineSegment(sketch, "E356", {"start": v(39.23, 152) * mm, "end": v(33.45, 142) * mm});
            skLineSegment(sketch, "E357", {"start": v(33.45, 142) * mm, "end": v(39.23, 132) * mm});
            skPoint(sketch, "E358", {"position": v(31.73, 153) * mm});
            skPoint(sketch, "E358.positionSnap0", {"position": v(31.73, 152) * mm});
            skPoint(sketch, "E359.positionSnap0", {"position": v(31.73, 132) * mm});
            skPoint(sketch, "E360", {"position": v(25.67, 136.5) * mm});
            skPoint(sketch, "E361", {"position": v(37.79, 136.5) * mm});
            skPoint(sketch, "E362", {"position": v(37.88, 147.67) * mm});
            skPoint(sketch, "E363", {"position": v(24.9, 148.85) * mm});
            skLineSegment(sketch, "E364", {"start": v(34.6, 142) * mm, "end": v(34.26, 142.6) * mm});
            skPoint(sketch, "E365", {"position": v(40.96, 153) * mm});
            skPoint(sketch, "E366", {"position": v(34.6, 142) * mm});
            skLineSegment(sketch, "E367", {"start": v(24.23, 154) * mm, "end": v(39.23, 154) * mm});
            skLineSegment(sketch, "E368", {"start": v(24.23, 174) * mm, "end": v(39.23, 174) * mm});
            skLineSegment(sketch, "E369", {"start": v(24.23, 174) * mm, "end": v(30, 164) * mm});
            skLineSegment(sketch, "E370", {"start": v(30, 164) * mm, "end": v(24.23, 154) * mm});
            skLineSegment(sketch, "E371", {"start": v(39.23, 174) * mm, "end": v(33.45, 164) * mm});
            skLineSegment(sketch, "E372", {"start": v(33.45, 164) * mm, "end": v(39.23, 154) * mm});
            skPoint(sketch, "E373", {"position": v(31.73, 175) * mm});
            skPoint(sketch, "E373.positionSnap0", {"position": v(31.73, 174) * mm});
            skPoint(sketch, "E374.positionSnap0", {"position": v(31.73, 154) * mm});
            skPoint(sketch, "E375", {"position": v(25.67, 158.5) * mm});
            skPoint(sketch, "E376", {"position": v(37.79, 158.5) * mm});
            skPoint(sketch, "E377", {"position": v(37.88, 169.67) * mm});
            skPoint(sketch, "E378", {"position": v(24.9, 170.85) * mm});
            skLineSegment(sketch, "E379", {"start": v(34.6, 164) * mm, "end": v(34.26, 164.6) * mm});
            skPoint(sketch, "E380", {"position": v(40.96, 175) * mm});
            skPoint(sketch, "E381", {"position": v(34.6, 164) * mm});
            skLineSegment(sketch, "E382", {"start": v(36.34, 11) * mm, "end": v(51.34, 11) * mm});
            skLineSegment(sketch, "E383", {"start": v(36.34, 31) * mm, "end": v(51.34, 31) * mm});
            skLineSegment(sketch, "E384", {"start": v(36.34, 31) * mm, "end": v(42.11, 21) * mm});
            skLineSegment(sketch, "E385", {"start": v(42.11, 21) * mm, "end": v(36.34, 11) * mm});
            skLineSegment(sketch, "E386", {"start": v(51.34, 31) * mm, "end": v(45.57, 21) * mm});
            skLineSegment(sketch, "E387", {"start": v(45.57, 21) * mm, "end": v(51.34, 11) * mm});
            skPoint(sketch, "E388", {"position": v(43.84, 32) * mm});
            skPoint(sketch, "E388.positionSnap0", {"position": v(43.84, 31) * mm});
            skPoint(sketch, "E389", {"position": v(43.84, 10) * mm});
            skPoint(sketch, "E389.positionSnap0", {"position": v(43.84, 11) * mm});
            skPoint(sketch, "E390", {"position": v(37.78, 15.5) * mm});
            skPoint(sketch, "E391", {"position": v(49.9, 15.5) * mm});
            skPoint(sketch, "E392", {"position": v(50, 26.67) * mm});
            skPoint(sketch, "E393", {"position": v(37, 27.85) * mm});
            skLineSegment(sketch, "E394", {"start": v(46.72, 21) * mm, "end": v(46.37, 21.6) * mm});
            skPoint(sketch, "E395", {"position": v(53.07, 32) * mm});
            skPoint(sketch, "E396", {"position": v(46.72, 21) * mm});
            skPoint(sketch, "E397", {"position": v(53.07, 10) * mm});
            skLineSegment(sketch, "E398", {"start": v(36.34, 33) * mm, "end": v(51.34, 33) * mm});
            skLineSegment(sketch, "E399", {"start": v(36.34, 53) * mm, "end": v(51.34, 53) * mm});
            skLineSegment(sketch, "E400", {"start": v(36.34, 53) * mm, "end": v(42.11, 43) * mm});
            skLineSegment(sketch, "E401", {"start": v(42.11, 43) * mm, "end": v(36.34, 33) * mm});
            skLineSegment(sketch, "E402", {"start": v(51.34, 53) * mm, "end": v(45.57, 43) * mm});
            skLineSegment(sketch, "E403", {"start": v(45.57, 43) * mm, "end": v(51.34, 33) * mm});
            skPoint(sketch, "E404", {"position": v(43.84, 54) * mm});
            skPoint(sketch, "E404.positionSnap0", {"position": v(43.84, 53) * mm});
            skPoint(sketch, "E405.positionSnap0", {"position": v(43.84, 33) * mm});
            skPoint(sketch, "E406", {"position": v(37.78, 37.5) * mm});
            skPoint(sketch, "E407", {"position": v(49.9, 37.5) * mm});
            skPoint(sketch, "E408", {"position": v(50, 48.67) * mm});
            skPoint(sketch, "E409", {"position": v(37, 49.85) * mm});
            skLineSegment(sketch, "E410", {"start": v(46.72, 43) * mm, "end": v(46.37, 43.6) * mm});
            skPoint(sketch, "E411", {"position": v(53.07, 54) * mm});
            skPoint(sketch, "E412", {"position": v(46.72, 43) * mm});
            skLineSegment(sketch, "E413", {"start": v(36.34, 55) * mm, "end": v(51.34, 55) * mm});
            skLineSegment(sketch, "E414", {"start": v(36.34, 75) * mm, "end": v(51.34, 75) * mm});
            skLineSegment(sketch, "E415", {"start": v(36.34, 75) * mm, "end": v(42.11, 65) * mm});
            skLineSegment(sketch, "E416", {"start": v(42.11, 65) * mm, "end": v(36.34, 55) * mm});
            skLineSegment(sketch, "E417", {"start": v(51.34, 75) * mm, "end": v(45.57, 65) * mm});
            skLineSegment(sketch, "E418", {"start": v(45.57, 65) * mm, "end": v(51.34, 55) * mm});
            skPoint(sketch, "E419", {"position": v(43.84, 76) * mm});
            skPoint(sketch, "E419.positionSnap0", {"position": v(43.84, 75) * mm});
            skPoint(sketch, "E420.positionSnap0", {"position": v(43.84, 55) * mm});
            skPoint(sketch, "E421", {"position": v(37.78, 59.5) * mm});
            skPoint(sketch, "E422", {"position": v(49.9, 59.5) * mm});
            skPoint(sketch, "E423", {"position": v(50, 70.67) * mm});
            skPoint(sketch, "E424", {"position": v(37, 71.85) * mm});
            skLineSegment(sketch, "E425", {"start": v(46.72, 65) * mm, "end": v(46.37, 65.6) * mm});
            skPoint(sketch, "E426", {"position": v(53.07, 76) * mm});
            skPoint(sketch, "E427", {"position": v(46.72, 65) * mm});
            skLineSegment(sketch, "E428", {"start": v(36.34, 77) * mm, "end": v(51.34, 77) * mm});
            skLineSegment(sketch, "E429", {"start": v(36.34, 97) * mm, "end": v(51.34, 97) * mm});
            skLineSegment(sketch, "E430", {"start": v(36.34, 97) * mm, "end": v(42.11, 87) * mm});
            skLineSegment(sketch, "E431", {"start": v(42.11, 87) * mm, "end": v(36.34, 77) * mm});
            skLineSegment(sketch, "E432", {"start": v(51.34, 97) * mm, "end": v(45.57, 87) * mm});
            skLineSegment(sketch, "E433", {"start": v(45.57, 87) * mm, "end": v(51.34, 77) * mm});
            skPoint(sketch, "E434", {"position": v(43.84, 98) * mm});
            skPoint(sketch, "E434.positionSnap0", {"position": v(43.84, 97) * mm});
            skPoint(sketch, "E435.positionSnap0", {"position": v(43.84, 77) * mm});
            skPoint(sketch, "E436", {"position": v(37.78, 81.5) * mm});
            skPoint(sketch, "E437", {"position": v(49.9, 81.5) * mm});
            skPoint(sketch, "E438", {"position": v(50, 92.67) * mm});
            skPoint(sketch, "E439", {"position": v(37, 93.85) * mm});
            skLineSegment(sketch, "E440", {"start": v(46.72, 87) * mm, "end": v(46.37, 87.6) * mm});
            skPoint(sketch, "E441", {"position": v(53.07, 98) * mm});
            skPoint(sketch, "E442", {"position": v(46.72, 87) * mm});
            skLineSegment(sketch, "E443", {"start": v(36.34, 99) * mm, "end": v(51.34, 99) * mm});
            skLineSegment(sketch, "E444", {"start": v(36.34, 119) * mm, "end": v(51.34, 119) * mm});
            skLineSegment(sketch, "E445", {"start": v(36.34, 119) * mm, "end": v(42.11, 109) * mm});
            skLineSegment(sketch, "E446", {"start": v(42.11, 109) * mm, "end": v(36.34, 99) * mm});
            skLineSegment(sketch, "E447", {"start": v(51.34, 119) * mm, "end": v(45.57, 109) * mm});
            skLineSegment(sketch, "E448", {"start": v(45.57, 109) * mm, "end": v(51.34, 99) * mm});
            skPoint(sketch, "E449", {"position": v(43.84, 120) * mm});
            skPoint(sketch, "E449.positionSnap0", {"position": v(43.84, 119) * mm});
            skPoint(sketch, "E450.positionSnap0", {"position": v(43.84, 99) * mm});
            skPoint(sketch, "E451", {"position": v(37.78, 103.5) * mm});
            skPoint(sketch, "E452", {"position": v(49.9, 103.5) * mm});
            skPoint(sketch, "E453", {"position": v(50, 114.67) * mm});
            skPoint(sketch, "E454", {"position": v(37, 115.85) * mm});
            skLineSegment(sketch, "E455", {"start": v(46.72, 109) * mm, "end": v(46.37, 109.6) * mm});
            skPoint(sketch, "E456", {"position": v(53.07, 120) * mm});
            skPoint(sketch, "E457", {"position": v(46.72, 109) * mm});
            skLineSegment(sketch, "E458", {"start": v(36.34, 121) * mm, "end": v(51.34, 121) * mm});
            skLineSegment(sketch, "E459", {"start": v(36.34, 141) * mm, "end": v(51.34, 141) * mm});
            skLineSegment(sketch, "E460", {"start": v(36.34, 141) * mm, "end": v(42.11, 131) * mm});
            skLineSegment(sketch, "E461", {"start": v(42.11, 131) * mm, "end": v(36.34, 121) * mm});
            skLineSegment(sketch, "E462", {"start": v(51.34, 141) * mm, "end": v(45.57, 131) * mm});
            skLineSegment(sketch, "E463", {"start": v(45.57, 131) * mm, "end": v(51.34, 121) * mm});
            skPoint(sketch, "E464", {"position": v(43.84, 142) * mm});
            skPoint(sketch, "E464.positionSnap0", {"position": v(43.84, 141) * mm});
            skPoint(sketch, "E465.positionSnap0", {"position": v(43.84, 121) * mm});
            skPoint(sketch, "E466", {"position": v(37.78, 125.5) * mm});
            skPoint(sketch, "E467", {"position": v(49.9, 125.5) * mm});
            skPoint(sketch, "E468", {"position": v(50, 136.67) * mm});
            skPoint(sketch, "E469", {"position": v(37, 137.85) * mm});
            skLineSegment(sketch, "E470", {"start": v(46.72, 131) * mm, "end": v(46.37, 131.6) * mm});
            skPoint(sketch, "E471", {"position": v(53.07, 142) * mm});
            skPoint(sketch, "E472", {"position": v(46.72, 131) * mm});
            skLineSegment(sketch, "E473", {"start": v(36.34, 143) * mm, "end": v(51.34, 143) * mm});
            skLineSegment(sketch, "E474", {"start": v(36.34, 163) * mm, "end": v(51.34, 163) * mm});
            skLineSegment(sketch, "E475", {"start": v(36.34, 163) * mm, "end": v(42.11, 153) * mm});
            skLineSegment(sketch, "E476", {"start": v(42.11, 153) * mm, "end": v(36.34, 143) * mm});
            skLineSegment(sketch, "E477", {"start": v(51.34, 163) * mm, "end": v(45.57, 153) * mm});
            skLineSegment(sketch, "E478", {"start": v(45.57, 153) * mm, "end": v(51.34, 143) * mm});
            skPoint(sketch, "E479", {"position": v(43.84, 164) * mm});
            skPoint(sketch, "E479.positionSnap0", {"position": v(43.84, 163) * mm});
            skPoint(sketch, "E480.positionSnap0", {"position": v(43.84, 143) * mm});
            skPoint(sketch, "E481", {"position": v(37.78, 147.5) * mm});
            skPoint(sketch, "E482", {"position": v(49.9, 147.5) * mm});
            skPoint(sketch, "E483", {"position": v(50, 158.67) * mm});
            skPoint(sketch, "E484", {"position": v(37, 159.85) * mm});
            skLineSegment(sketch, "E485", {"start": v(46.72, 153) * mm, "end": v(46.37, 153.6) * mm});
            skPoint(sketch, "E486", {"position": v(53.07, 164) * mm});
            skPoint(sketch, "E487", {"position": v(46.72, 153) * mm});
            skLineSegment(sketch, "E488", {"start": v(36.34, 165) * mm, "end": v(51.34, 165) * mm});
            skLineSegment(sketch, "E489", {"start": v(36.34, 185) * mm, "end": v(51.34, 185) * mm});
            skLineSegment(sketch, "E490", {"start": v(36.34, 185) * mm, "end": v(42.11, 175) * mm});
            skLineSegment(sketch, "E491", {"start": v(42.11, 175) * mm, "end": v(36.34, 165) * mm});
            skLineSegment(sketch, "E492", {"start": v(51.34, 185) * mm, "end": v(45.57, 175) * mm});
            skLineSegment(sketch, "E493", {"start": v(45.57, 175) * mm, "end": v(51.34, 165) * mm});
            skPoint(sketch, "E494", {"position": v(43.84, 186) * mm});
            skPoint(sketch, "E494.positionSnap0", {"position": v(43.84, 185) * mm});
            skPoint(sketch, "E495.positionSnap0", {"position": v(43.84, 165) * mm});
            skPoint(sketch, "E496", {"position": v(37.78, 169.5) * mm});
            skPoint(sketch, "E497", {"position": v(49.9, 169.5) * mm});
            skPoint(sketch, "E498", {"position": v(50, 180.67) * mm});
            skPoint(sketch, "E499", {"position": v(37, 181.85) * mm});
            skLineSegment(sketch, "E500", {"start": v(46.72, 175) * mm, "end": v(46.37, 175.6) * mm});
            skPoint(sketch, "E501", {"position": v(34.6, 186) * mm});
            skPoint(sketch, "E502", {"position": v(53.07, 186) * mm});
            skPoint(sketch, "E503", {"position": v(46.72, 175) * mm});
            skLineSegment(sketch, "E504", {"start": v(48.45, 0) * mm, "end": v(63.45, 0) * mm});
            skLineSegment(sketch, "E505", {"start": v(48.45, 20) * mm, "end": v(63.45, 20) * mm});
            skLineSegment(sketch, "E506", {"start": v(48.45, 20) * mm, "end": v(54.23, 10) * mm});
            skLineSegment(sketch, "E507", {"start": v(54.23, 10) * mm, "end": v(48.45, 0) * mm});
            skLineSegment(sketch, "E508", {"start": v(63.45, 20) * mm, "end": v(57.68, 10) * mm});
            skLineSegment(sketch, "E509", {"start": v(57.68, 10) * mm, "end": v(63.45, 0) * mm});
            skPoint(sketch, "E510", {"position": v(55.95, 21) * mm});
            skPoint(sketch, "E510.positionSnap0", {"position": v(55.95, 20) * mm});
            skPoint(sketch, "E511", {"position": v(55.95, -1) * mm});
            skPoint(sketch, "E511.positionSnap0", {"position": v(55.95, 0) * mm});
            skPoint(sketch, "E512", {"position": v(49.9, 4.5) * mm});
            skPoint(sketch, "E513", {"position": v(62.01, 4.5) * mm});
            skPoint(sketch, "E514", {"position": v(62.1, 15.67) * mm});
            skPoint(sketch, "E515", {"position": v(49.12, 16.85) * mm});
            skLineSegment(sketch, "E516", {"start": v(58.83, 10) * mm, "end": v(58.49, 10.6) * mm});
            skPoint(sketch, "E517", {"position": v(65.19, 21) * mm});
            skPoint(sketch, "E518", {"position": v(58.83, 10) * mm});
            skPoint(sketch, "E519", {"position": v(46.72, -1) * mm});
            skPoint(sketch, "E520", {"position": v(65.19, -1) * mm});
            skLineSegment(sketch, "E521", {"start": v(48.45, 22) * mm, "end": v(63.45, 22) * mm});
            skLineSegment(sketch, "E522", {"start": v(48.45, 42) * mm, "end": v(63.45, 42) * mm});
            skLineSegment(sketch, "E523", {"start": v(48.45, 42) * mm, "end": v(54.23, 32) * mm});
            skLineSegment(sketch, "E524", {"start": v(54.23, 32) * mm, "end": v(48.45, 22) * mm});
            skLineSegment(sketch, "E525", {"start": v(63.45, 42) * mm, "end": v(57.68, 32) * mm});
            skLineSegment(sketch, "E526", {"start": v(57.68, 32) * mm, "end": v(63.45, 22) * mm});
            skPoint(sketch, "E527", {"position": v(55.95, 43) * mm});
            skPoint(sketch, "E527.positionSnap0", {"position": v(55.95, 42) * mm});
            skPoint(sketch, "E528.positionSnap0", {"position": v(55.95, 22) * mm});
            skPoint(sketch, "E529", {"position": v(49.9, 26.5) * mm});
            skPoint(sketch, "E530", {"position": v(62.01, 26.5) * mm});
            skPoint(sketch, "E531", {"position": v(62.1, 37.67) * mm});
            skPoint(sketch, "E532", {"position": v(49.12, 38.85) * mm});
            skLineSegment(sketch, "E533", {"start": v(58.83, 32) * mm, "end": v(58.49, 32.6) * mm});
            skPoint(sketch, "E534", {"position": v(65.19, 43) * mm});
            skPoint(sketch, "E535", {"position": v(58.83, 32) * mm});
            skLineSegment(sketch, "E536", {"start": v(48.45, 44) * mm, "end": v(63.45, 44) * mm});
            skLineSegment(sketch, "E537", {"start": v(48.45, 64) * mm, "end": v(63.45, 64) * mm});
            skLineSegment(sketch, "E538", {"start": v(48.45, 64) * mm, "end": v(54.23, 54) * mm});
            skLineSegment(sketch, "E539", {"start": v(54.23, 54) * mm, "end": v(48.45, 44) * mm});
            skLineSegment(sketch, "E540", {"start": v(63.45, 64) * mm, "end": v(57.68, 54) * mm});
            skLineSegment(sketch, "E541", {"start": v(57.68, 54) * mm, "end": v(63.45, 44) * mm});
            skPoint(sketch, "E542", {"position": v(55.95, 65) * mm});
            skPoint(sketch, "E542.positionSnap0", {"position": v(55.95, 64) * mm});
            skPoint(sketch, "E543.positionSnap0", {"position": v(55.95, 44) * mm});
            skPoint(sketch, "E544", {"position": v(49.9, 48.5) * mm});
            skPoint(sketch, "E545", {"position": v(62.01, 48.5) * mm});
            skPoint(sketch, "E546", {"position": v(62.1, 59.67) * mm});
            skPoint(sketch, "E547", {"position": v(49.12, 60.85) * mm});
            skLineSegment(sketch, "E548", {"start": v(58.83, 54) * mm, "end": v(58.49, 54.6) * mm});
            skPoint(sketch, "E549", {"position": v(65.19, 65) * mm});
            skPoint(sketch, "E550", {"position": v(58.83, 54) * mm});
            skLineSegment(sketch, "E551", {"start": v(48.45, 66) * mm, "end": v(63.45, 66) * mm});
            skLineSegment(sketch, "E552", {"start": v(48.45, 86) * mm, "end": v(63.45, 86) * mm});
            skLineSegment(sketch, "E553", {"start": v(48.45, 86) * mm, "end": v(54.23, 76) * mm});
            skLineSegment(sketch, "E554", {"start": v(54.23, 76) * mm, "end": v(48.45, 66) * mm});
            skLineSegment(sketch, "E555", {"start": v(63.45, 86) * mm, "end": v(57.68, 76) * mm});
            skLineSegment(sketch, "E556", {"start": v(57.68, 76) * mm, "end": v(63.45, 66) * mm});
            skPoint(sketch, "E557", {"position": v(55.95, 87) * mm});
            skPoint(sketch, "E557.positionSnap0", {"position": v(55.95, 86) * mm});
            skPoint(sketch, "E558.positionSnap0", {"position": v(55.95, 66) * mm});
            skPoint(sketch, "E559", {"position": v(49.9, 70.5) * mm});
            skPoint(sketch, "E560", {"position": v(62.01, 70.5) * mm});
            skPoint(sketch, "E561", {"position": v(62.1, 81.67) * mm});
            skPoint(sketch, "E562", {"position": v(49.12, 82.85) * mm});
            skLineSegment(sketch, "E563", {"start": v(58.83, 76) * mm, "end": v(58.49, 76.6) * mm});
            skPoint(sketch, "E564", {"position": v(65.19, 87) * mm});
            skPoint(sketch, "E565", {"position": v(58.83, 76) * mm});
            skLineSegment(sketch, "E566", {"start": v(48.45, 88) * mm, "end": v(63.45, 88) * mm});
            skLineSegment(sketch, "E567", {"start": v(48.45, 108) * mm, "end": v(63.45, 108) * mm});
            skLineSegment(sketch, "E568", {"start": v(48.45, 108) * mm, "end": v(54.23, 98) * mm});
            skLineSegment(sketch, "E569", {"start": v(54.23, 98) * mm, "end": v(48.45, 88) * mm});
            skLineSegment(sketch, "E570", {"start": v(63.45, 108) * mm, "end": v(57.68, 98) * mm});
            skLineSegment(sketch, "E571", {"start": v(57.68, 98) * mm, "end": v(63.45, 88) * mm});
            skPoint(sketch, "E572", {"position": v(55.95, 109) * mm});
            skPoint(sketch, "E572.positionSnap0", {"position": v(55.95, 108) * mm});
            skPoint(sketch, "E573.positionSnap0", {"position": v(55.95, 88) * mm});
            skPoint(sketch, "E574", {"position": v(49.9, 92.5) * mm});
            skPoint(sketch, "E575", {"position": v(62.01, 92.5) * mm});
            skPoint(sketch, "E576", {"position": v(62.1, 103.67) * mm});
            skPoint(sketch, "E577", {"position": v(49.12, 104.85) * mm});
            skLineSegment(sketch, "E578", {"start": v(58.83, 98) * mm, "end": v(58.49, 98.6) * mm});
            skPoint(sketch, "E579", {"position": v(65.19, 109) * mm});
            skPoint(sketch, "E580", {"position": v(58.83, 98) * mm});
            skLineSegment(sketch, "E581", {"start": v(48.45, 110) * mm, "end": v(63.45, 110) * mm});
            skLineSegment(sketch, "E582", {"start": v(48.45, 130) * mm, "end": v(63.45, 130) * mm});
            skLineSegment(sketch, "E583", {"start": v(48.45, 130) * mm, "end": v(54.23, 120) * mm});
            skLineSegment(sketch, "E584", {"start": v(54.23, 120) * mm, "end": v(48.45, 110) * mm});
            skLineSegment(sketch, "E585", {"start": v(63.45, 130) * mm, "end": v(57.68, 120) * mm});
            skLineSegment(sketch, "E586", {"start": v(57.68, 120) * mm, "end": v(63.45, 110) * mm});
            skPoint(sketch, "E587", {"position": v(55.95, 131) * mm});
            skPoint(sketch, "E587.positionSnap0", {"position": v(55.95, 130) * mm});
            skPoint(sketch, "E588.positionSnap0", {"position": v(55.95, 110) * mm});
            skPoint(sketch, "E589", {"position": v(49.9, 114.5) * mm});
            skPoint(sketch, "E590", {"position": v(62.01, 114.5) * mm});
            skPoint(sketch, "E591", {"position": v(62.1, 125.67) * mm});
            skPoint(sketch, "E592", {"position": v(49.12, 126.85) * mm});
            skLineSegment(sketch, "E593", {"start": v(58.83, 120) * mm, "end": v(58.49, 120.6) * mm});
            skPoint(sketch, "E594", {"position": v(65.19, 131) * mm});
            skPoint(sketch, "E595", {"position": v(58.83, 120) * mm});
            skLineSegment(sketch, "E596", {"start": v(48.45, 132) * mm, "end": v(63.45, 132) * mm});
            skLineSegment(sketch, "E597", {"start": v(48.45, 152) * mm, "end": v(63.45, 152) * mm});
            skLineSegment(sketch, "E598", {"start": v(48.45, 152) * mm, "end": v(54.23, 142) * mm});
            skLineSegment(sketch, "E599", {"start": v(54.23, 142) * mm, "end": v(48.45, 132) * mm});
            skLineSegment(sketch, "E600", {"start": v(63.45, 152) * mm, "end": v(57.68, 142) * mm});
            skLineSegment(sketch, "E601", {"start": v(57.68, 142) * mm, "end": v(63.45, 132) * mm});
            skPoint(sketch, "E602", {"position": v(55.95, 153) * mm});
            skPoint(sketch, "E602.positionSnap0", {"position": v(55.95, 152) * mm});
            skPoint(sketch, "E603.positionSnap0", {"position": v(55.95, 132) * mm});
            skPoint(sketch, "E604", {"position": v(49.9, 136.5) * mm});
            skPoint(sketch, "E605", {"position": v(62.01, 136.5) * mm});
            skPoint(sketch, "E606", {"position": v(62.1, 147.67) * mm});
            skPoint(sketch, "E607", {"position": v(49.12, 148.85) * mm});
            skLineSegment(sketch, "E608", {"start": v(58.83, 142) * mm, "end": v(58.49, 142.6) * mm});
            skPoint(sketch, "E609", {"position": v(65.19, 153) * mm});
            skPoint(sketch, "E610", {"position": v(58.83, 142) * mm});
            skLineSegment(sketch, "E611", {"start": v(48.45, 154) * mm, "end": v(63.45, 154) * mm});
            skLineSegment(sketch, "E612", {"start": v(48.45, 174) * mm, "end": v(63.45, 174) * mm});
            skLineSegment(sketch, "E613", {"start": v(48.45, 174) * mm, "end": v(54.23, 164) * mm});
            skLineSegment(sketch, "E614", {"start": v(54.23, 164) * mm, "end": v(48.45, 154) * mm});
            skLineSegment(sketch, "E615", {"start": v(63.45, 174) * mm, "end": v(57.68, 164) * mm});
            skLineSegment(sketch, "E616", {"start": v(57.68, 164) * mm, "end": v(63.45, 154) * mm});
            skPoint(sketch, "E617", {"position": v(55.95, 175) * mm});
            skPoint(sketch, "E617.positionSnap0", {"position": v(55.95, 174) * mm});
            skPoint(sketch, "E618.positionSnap0", {"position": v(55.95, 154) * mm});
            skPoint(sketch, "E619", {"position": v(49.9, 158.5) * mm});
            skPoint(sketch, "E620", {"position": v(62.01, 158.5) * mm});
            skPoint(sketch, "E621", {"position": v(62.1, 169.67) * mm});
            skPoint(sketch, "E622", {"position": v(49.12, 170.85) * mm});
            skLineSegment(sketch, "E623", {"start": v(58.83, 164) * mm, "end": v(58.49, 164.6) * mm});
            skPoint(sketch, "E624", {"position": v(65.19, 175) * mm});
            skPoint(sketch, "E625", {"position": v(58.83, 164) * mm});
            skLineSegment(sketch, "E626", {"start": v(60.57, 11) * mm, "end": v(75.57, 11) * mm});
            skLineSegment(sketch, "E627", {"start": v(60.57, 31) * mm, "end": v(75.57, 31) * mm});
            skLineSegment(sketch, "E628", {"start": v(60.57, 31) * mm, "end": v(66.34, 21) * mm});
            skLineSegment(sketch, "E629", {"start": v(66.34, 21) * mm, "end": v(60.57, 11) * mm});
            skLineSegment(sketch, "E630", {"start": v(75.57, 31) * mm, "end": v(69.8, 21) * mm});
            skLineSegment(sketch, "E631", {"start": v(69.8, 21) * mm, "end": v(75.57, 11) * mm});
            skPoint(sketch, "E632", {"position": v(68.07, 32) * mm});
            skPoint(sketch, "E632.positionSnap0", {"position": v(68.07, 31) * mm});
            skPoint(sketch, "E633", {"position": v(68.07, 10) * mm});
            skPoint(sketch, "E633.positionSnap0", {"position": v(68.07, 11) * mm});
            skPoint(sketch, "E634", {"position": v(62, 15.5) * mm});
            skPoint(sketch, "E635", {"position": v(74.13, 15.5) * mm});
            skPoint(sketch, "E636", {"position": v(74.22, 26.67) * mm});
            skPoint(sketch, "E637", {"position": v(61.23, 27.85) * mm});
            skLineSegment(sketch, "E638", {"start": v(70.95, 21) * mm, "end": v(70.6, 21.6) * mm});
            skPoint(sketch, "E639", {"position": v(77.3, 32) * mm});
            skPoint(sketch, "E640", {"position": v(70.95, 21) * mm});
            skPoint(sketch, "E641", {"position": v(77.3, 10) * mm});
            skLineSegment(sketch, "E642", {"start": v(60.57, 33) * mm, "end": v(75.57, 33) * mm});
            skLineSegment(sketch, "E643", {"start": v(60.57, 53) * mm, "end": v(75.57, 53) * mm});
            skLineSegment(sketch, "E644", {"start": v(60.57, 53) * mm, "end": v(66.34, 43) * mm});
            skLineSegment(sketch, "E645", {"start": v(66.34, 43) * mm, "end": v(60.57, 33) * mm});
            skLineSegment(sketch, "E646", {"start": v(75.57, 53) * mm, "end": v(69.8, 43) * mm});
            skLineSegment(sketch, "E647", {"start": v(69.8, 43) * mm, "end": v(75.57, 33) * mm});
            skPoint(sketch, "E648", {"position": v(68.07, 54) * mm});
            skPoint(sketch, "E648.positionSnap0", {"position": v(68.07, 53) * mm});
            skPoint(sketch, "E649.positionSnap0", {"position": v(68.07, 33) * mm});
            skPoint(sketch, "E650", {"position": v(62, 37.5) * mm});
            skPoint(sketch, "E651", {"position": v(74.13, 37.5) * mm});
            skPoint(sketch, "E652", {"position": v(74.22, 48.67) * mm});
            skPoint(sketch, "E653", {"position": v(61.23, 49.85) * mm});
            skLineSegment(sketch, "E654", {"start": v(70.95, 43) * mm, "end": v(70.6, 43.6) * mm});
            skPoint(sketch, "E655", {"position": v(77.3, 54) * mm});
            skPoint(sketch, "E656", {"position": v(70.95, 43) * mm});
            skLineSegment(sketch, "E657", {"start": v(60.57, 55) * mm, "end": v(75.57, 55) * mm});
            skLineSegment(sketch, "E658", {"start": v(60.57, 75) * mm, "end": v(75.57, 75) * mm});
            skLineSegment(sketch, "E659", {"start": v(60.57, 75) * mm, "end": v(66.34, 65) * mm});
            skLineSegment(sketch, "E660", {"start": v(66.34, 65) * mm, "end": v(60.57, 55) * mm});
            skLineSegment(sketch, "E661", {"start": v(75.57, 75) * mm, "end": v(69.8, 65) * mm});
            skLineSegment(sketch, "E662", {"start": v(69.8, 65) * mm, "end": v(75.57, 55) * mm});
            skPoint(sketch, "E663", {"position": v(68.07, 76) * mm});
            skPoint(sketch, "E663.positionSnap0", {"position": v(68.07, 75) * mm});
            skPoint(sketch, "E664.positionSnap0", {"position": v(68.07, 55) * mm});
            skPoint(sketch, "E665", {"position": v(62, 59.5) * mm});
            skPoint(sketch, "E666", {"position": v(74.13, 59.5) * mm});
            skPoint(sketch, "E667", {"position": v(74.22, 70.67) * mm});
            skPoint(sketch, "E668", {"position": v(61.23, 71.85) * mm});
            skLineSegment(sketch, "E669", {"start": v(70.95, 65) * mm, "end": v(70.6, 65.6) * mm});
            skPoint(sketch, "E670", {"position": v(77.3, 76) * mm});
            skPoint(sketch, "E671", {"position": v(70.95, 65) * mm});
            skLineSegment(sketch, "E672", {"start": v(60.57, 77) * mm, "end": v(75.57, 77) * mm});
            skLineSegment(sketch, "E673", {"start": v(60.57, 97) * mm, "end": v(75.57, 97) * mm});
            skLineSegment(sketch, "E674", {"start": v(60.57, 97) * mm, "end": v(66.34, 87) * mm});
            skLineSegment(sketch, "E675", {"start": v(66.34, 87) * mm, "end": v(60.57, 77) * mm});
            skLineSegment(sketch, "E676", {"start": v(75.57, 97) * mm, "end": v(69.8, 87) * mm});
            skLineSegment(sketch, "E677", {"start": v(69.8, 87) * mm, "end": v(75.57, 77) * mm});
            skPoint(sketch, "E678", {"position": v(68.07, 98) * mm});
            skPoint(sketch, "E678.positionSnap0", {"position": v(68.07, 97) * mm});
            skPoint(sketch, "E679.positionSnap0", {"position": v(68.07, 77) * mm});
            skPoint(sketch, "E680", {"position": v(62, 81.5) * mm});
            skPoint(sketch, "E681", {"position": v(74.13, 81.5) * mm});
            skPoint(sketch, "E682", {"position": v(74.22, 92.67) * mm});
            skPoint(sketch, "E683", {"position": v(61.23, 93.85) * mm});
            skLineSegment(sketch, "E684", {"start": v(70.95, 87) * mm, "end": v(70.6, 87.6) * mm});
            skPoint(sketch, "E685", {"position": v(77.3, 98) * mm});
            skPoint(sketch, "E686", {"position": v(70.95, 87) * mm});
            skLineSegment(sketch, "E687", {"start": v(60.57, 99) * mm, "end": v(75.57, 99) * mm});
            skLineSegment(sketch, "E688", {"start": v(60.57, 119) * mm, "end": v(75.57, 119) * mm});
            skLineSegment(sketch, "E689", {"start": v(60.57, 119) * mm, "end": v(66.34, 109) * mm});
            skLineSegment(sketch, "E690", {"start": v(66.34, 109) * mm, "end": v(60.57, 99) * mm});
            skLineSegment(sketch, "E691", {"start": v(75.57, 119) * mm, "end": v(69.8, 109) * mm});
            skLineSegment(sketch, "E692", {"start": v(69.8, 109) * mm, "end": v(75.57, 99) * mm});
            skPoint(sketch, "E693", {"position": v(68.07, 120) * mm});
            skPoint(sketch, "E693.positionSnap0", {"position": v(68.07, 119) * mm});
            skPoint(sketch, "E694.positionSnap0", {"position": v(68.07, 99) * mm});
            skPoint(sketch, "E695", {"position": v(62, 103.5) * mm});
            skPoint(sketch, "E696", {"position": v(74.13, 103.5) * mm});
            skPoint(sketch, "E697", {"position": v(74.22, 114.67) * mm});
            skPoint(sketch, "E698", {"position": v(61.23, 115.85) * mm});
            skLineSegment(sketch, "E699", {"start": v(70.95, 109) * mm, "end": v(70.6, 109.6) * mm});
            skPoint(sketch, "E700", {"position": v(77.3, 120) * mm});
            skPoint(sketch, "E701", {"position": v(70.95, 109) * mm});
            skLineSegment(sketch, "E702", {"start": v(60.57, 121) * mm, "end": v(75.57, 121) * mm});
            skLineSegment(sketch, "E703", {"start": v(60.57, 141) * mm, "end": v(75.57, 141) * mm});
            skLineSegment(sketch, "E704", {"start": v(60.57, 141) * mm, "end": v(66.34, 131) * mm});
            skLineSegment(sketch, "E705", {"start": v(66.34, 131) * mm, "end": v(60.57, 121) * mm});
            skLineSegment(sketch, "E706", {"start": v(75.57, 141) * mm, "end": v(69.8, 131) * mm});
            skLineSegment(sketch, "E707", {"start": v(69.8, 131) * mm, "end": v(75.57, 121) * mm});
            skPoint(sketch, "E708", {"position": v(68.07, 142) * mm});
            skPoint(sketch, "E708.positionSnap0", {"position": v(68.07, 141) * mm});
            skPoint(sketch, "E709.positionSnap0", {"position": v(68.07, 121) * mm});
            skPoint(sketch, "E710", {"position": v(62, 125.5) * mm});
            skPoint(sketch, "E711", {"position": v(74.13, 125.5) * mm});
            skPoint(sketch, "E712", {"position": v(74.22, 136.67) * mm});
            skPoint(sketch, "E713", {"position": v(61.23, 137.85) * mm});
            skLineSegment(sketch, "E714", {"start": v(70.95, 131) * mm, "end": v(70.6, 131.6) * mm});
            skPoint(sketch, "E715", {"position": v(77.3, 142) * mm});
            skPoint(sketch, "E716", {"position": v(70.95, 131) * mm});
            skLineSegment(sketch, "E717", {"start": v(60.57, 143) * mm, "end": v(75.57, 143) * mm});
            skLineSegment(sketch, "E718", {"start": v(60.57, 163) * mm, "end": v(75.57, 163) * mm});
            skLineSegment(sketch, "E719", {"start": v(60.57, 163) * mm, "end": v(66.34, 153) * mm});
            skLineSegment(sketch, "E720", {"start": v(66.34, 153) * mm, "end": v(60.57, 143) * mm});
            skLineSegment(sketch, "E721", {"start": v(75.57, 163) * mm, "end": v(69.8, 153) * mm});
            skLineSegment(sketch, "E722", {"start": v(69.8, 153) * mm, "end": v(75.57, 143) * mm});
            skPoint(sketch, "E723", {"position": v(68.07, 164) * mm});
            skPoint(sketch, "E723.positionSnap0", {"position": v(68.07, 163) * mm});
            skPoint(sketch, "E724.positionSnap0", {"position": v(68.07, 143) * mm});
            skPoint(sketch, "E725", {"position": v(62, 147.5) * mm});
            skPoint(sketch, "E726", {"position": v(74.13, 147.5) * mm});
            skPoint(sketch, "E727", {"position": v(74.22, 158.67) * mm});
            skPoint(sketch, "E728", {"position": v(61.23, 159.85) * mm});
            skLineSegment(sketch, "E729", {"start": v(70.95, 153) * mm, "end": v(70.6, 153.6) * mm});
            skPoint(sketch, "E730", {"position": v(77.3, 164) * mm});
            skPoint(sketch, "E731", {"position": v(70.95, 153) * mm});
            skLineSegment(sketch, "E732", {"start": v(60.57, 165) * mm, "end": v(75.57, 165) * mm});
            skLineSegment(sketch, "E733", {"start": v(60.57, 185) * mm, "end": v(75.57, 185) * mm});
            skLineSegment(sketch, "E734", {"start": v(60.57, 185) * mm, "end": v(66.34, 175) * mm});
            skLineSegment(sketch, "E735", {"start": v(66.34, 175) * mm, "end": v(60.57, 165) * mm});
            skLineSegment(sketch, "E736", {"start": v(75.57, 185) * mm, "end": v(69.8, 175) * mm});
            skLineSegment(sketch, "E737", {"start": v(69.8, 175) * mm, "end": v(75.57, 165) * mm});
            skPoint(sketch, "E738", {"position": v(68.07, 186) * mm});
            skPoint(sketch, "E738.positionSnap0", {"position": v(68.07, 185) * mm});
            skPoint(sketch, "E739.positionSnap0", {"position": v(68.07, 165) * mm});
            skPoint(sketch, "E740", {"position": v(62, 169.5) * mm});
            skPoint(sketch, "E741", {"position": v(74.13, 169.5) * mm});
            skPoint(sketch, "E742", {"position": v(74.22, 180.67) * mm});
            skPoint(sketch, "E743", {"position": v(61.23, 181.85) * mm});
            skLineSegment(sketch, "E744", {"start": v(70.95, 175) * mm, "end": v(70.6, 175.6) * mm});
            skPoint(sketch, "E745", {"position": v(58.83, 186) * mm});
            skPoint(sketch, "E746", {"position": v(77.3, 186) * mm});
            skPoint(sketch, "E747", {"position": v(70.95, 175) * mm});
            skLineSegment(sketch, "E748", {"start": v(72.68, 0) * mm, "end": v(87.68, 0) * mm});
            skLineSegment(sketch, "E749", {"start": v(72.68, 20) * mm, "end": v(87.68, 20) * mm});
            skLineSegment(sketch, "E750", {"start": v(72.68, 20) * mm, "end": v(78.45, 10) * mm});
            skLineSegment(sketch, "E751", {"start": v(78.45, 10) * mm, "end": v(72.68, 0) * mm});
            skLineSegment(sketch, "E752", {"start": v(87.68, 20) * mm, "end": v(81.9, 10) * mm});
            skLineSegment(sketch, "E753", {"start": v(81.9, 10) * mm, "end": v(87.68, 0) * mm});
            skPoint(sketch, "E754", {"position": v(80.18, 21) * mm});
            skPoint(sketch, "E754.positionSnap0", {"position": v(80.18, 20) * mm});
            skPoint(sketch, "E755", {"position": v(80.18, -1) * mm});
            skPoint(sketch, "E755.positionSnap0", {"position": v(80.18, 0) * mm});
            skPoint(sketch, "E756", {"position": v(74.12, 4.5) * mm});
            skPoint(sketch, "E757", {"position": v(86.24, 4.5) * mm});
            skPoint(sketch, "E758", {"position": v(86.34, 15.67) * mm});
            skPoint(sketch, "E759", {"position": v(73.34, 16.85) * mm});
            skLineSegment(sketch, "E760", {"start": v(83.06, 10) * mm, "end": v(82.71, 10.6) * mm});
            skPoint(sketch, "E761", {"position": v(89.41, 21) * mm});
            skPoint(sketch, "E762", {"position": v(83.06, 10) * mm});
            skPoint(sketch, "E763", {"position": v(70.95, -1) * mm});
            skPoint(sketch, "E764", {"position": v(89.41, -1) * mm});
            skLineSegment(sketch, "E765", {"start": v(72.68, 22) * mm, "end": v(87.68, 22) * mm});
            skLineSegment(sketch, "E766", {"start": v(72.68, 42) * mm, "end": v(87.68, 42) * mm});
            skLineSegment(sketch, "E767", {"start": v(72.68, 42) * mm, "end": v(78.45, 32) * mm});
            skLineSegment(sketch, "E768", {"start": v(78.45, 32) * mm, "end": v(72.68, 22) * mm});
            skLineSegment(sketch, "E769", {"start": v(87.68, 42) * mm, "end": v(81.9, 32) * mm});
            skLineSegment(sketch, "E770", {"start": v(81.9, 32) * mm, "end": v(87.68, 22) * mm});
            skPoint(sketch, "E771", {"position": v(80.18, 43) * mm});
            skPoint(sketch, "E771.positionSnap0", {"position": v(80.18, 42) * mm});
            skPoint(sketch, "E772.positionSnap0", {"position": v(80.18, 22) * mm});
            skPoint(sketch, "E773", {"position": v(74.12, 26.5) * mm});
            skPoint(sketch, "E774", {"position": v(86.24, 26.5) * mm});
            skPoint(sketch, "E775", {"position": v(86.34, 37.67) * mm});
            skPoint(sketch, "E776", {"position": v(73.34, 38.85) * mm});
            skLineSegment(sketch, "E777", {"start": v(83.06, 32) * mm, "end": v(82.71, 32.6) * mm});
            skPoint(sketch, "E778", {"position": v(89.41, 43) * mm});
            skPoint(sketch, "E779", {"position": v(83.06, 32) * mm});
            skLineSegment(sketch, "E780", {"start": v(72.68, 44) * mm, "end": v(87.68, 44) * mm});
            skLineSegment(sketch, "E781", {"start": v(72.68, 64) * mm, "end": v(87.68, 64) * mm});
            skLineSegment(sketch, "E782", {"start": v(72.68, 64) * mm, "end": v(78.45, 54) * mm});
            skLineSegment(sketch, "E783", {"start": v(78.45, 54) * mm, "end": v(72.68, 44) * mm});
            skLineSegment(sketch, "E784", {"start": v(87.68, 64) * mm, "end": v(81.9, 54) * mm});
            skLineSegment(sketch, "E785", {"start": v(81.9, 54) * mm, "end": v(87.68, 44) * mm});
            skPoint(sketch, "E786", {"position": v(80.18, 65) * mm});
            skPoint(sketch, "E786.positionSnap0", {"position": v(80.18, 64) * mm});
            skPoint(sketch, "E787.positionSnap0", {"position": v(80.18, 44) * mm});
            skPoint(sketch, "E788", {"position": v(74.12, 48.5) * mm});
            skPoint(sketch, "E789", {"position": v(86.24, 48.5) * mm});
            skPoint(sketch, "E790", {"position": v(86.34, 59.67) * mm});
            skPoint(sketch, "E791", {"position": v(73.34, 60.85) * mm});
            skLineSegment(sketch, "E792", {"start": v(83.06, 54) * mm, "end": v(82.71, 54.6) * mm});
            skPoint(sketch, "E793", {"position": v(89.41, 65) * mm});
            skPoint(sketch, "E794", {"position": v(83.06, 54) * mm});
            skLineSegment(sketch, "E795", {"start": v(72.68, 66) * mm, "end": v(87.68, 66) * mm});
            skLineSegment(sketch, "E796", {"start": v(72.68, 86) * mm, "end": v(87.68, 86) * mm});
            skLineSegment(sketch, "E797", {"start": v(72.68, 86) * mm, "end": v(78.45, 76) * mm});
            skLineSegment(sketch, "E798", {"start": v(78.45, 76) * mm, "end": v(72.68, 66) * mm});
            skLineSegment(sketch, "E799", {"start": v(87.68, 86) * mm, "end": v(81.9, 76) * mm});
            skLineSegment(sketch, "E800", {"start": v(81.9, 76) * mm, "end": v(87.68, 66) * mm});
            skPoint(sketch, "E801", {"position": v(80.18, 87) * mm});
            skPoint(sketch, "E801.positionSnap0", {"position": v(80.18, 86) * mm});
            skPoint(sketch, "E802.positionSnap0", {"position": v(80.18, 66) * mm});
            skPoint(sketch, "E803", {"position": v(74.12, 70.5) * mm});
            skPoint(sketch, "E804", {"position": v(86.24, 70.5) * mm});
            skPoint(sketch, "E805", {"position": v(86.34, 81.67) * mm});
            skPoint(sketch, "E806", {"position": v(73.34, 82.85) * mm});
            skLineSegment(sketch, "E807", {"start": v(83.06, 76) * mm, "end": v(82.71, 76.6) * mm});
            skPoint(sketch, "E808", {"position": v(89.41, 87) * mm});
            skPoint(sketch, "E809", {"position": v(83.06, 76) * mm});
            skLineSegment(sketch, "E810", {"start": v(72.68, 88) * mm, "end": v(87.68, 88) * mm});
            skLineSegment(sketch, "E811", {"start": v(72.68, 108) * mm, "end": v(87.68, 108) * mm});
            skLineSegment(sketch, "E812", {"start": v(72.68, 108) * mm, "end": v(78.45, 98) * mm});
            skLineSegment(sketch, "E813", {"start": v(78.45, 98) * mm, "end": v(72.68, 88) * mm});
            skLineSegment(sketch, "E814", {"start": v(87.68, 108) * mm, "end": v(81.9, 98) * mm});
            skLineSegment(sketch, "E815", {"start": v(81.9, 98) * mm, "end": v(87.68, 88) * mm});
            skPoint(sketch, "E816", {"position": v(80.18, 109) * mm});
            skPoint(sketch, "E816.positionSnap0", {"position": v(80.18, 108) * mm});
            skPoint(sketch, "E817.positionSnap0", {"position": v(80.18, 88) * mm});
            skPoint(sketch, "E818", {"position": v(74.12, 92.5) * mm});
            skPoint(sketch, "E819", {"position": v(86.24, 92.5) * mm});
            skPoint(sketch, "E820", {"position": v(86.34, 103.67) * mm});
            skPoint(sketch, "E821", {"position": v(73.34, 104.85) * mm});
            skLineSegment(sketch, "E822", {"start": v(83.06, 98) * mm, "end": v(82.71, 98.6) * mm});
            skPoint(sketch, "E823", {"position": v(89.41, 109) * mm});
            skPoint(sketch, "E824", {"position": v(83.06, 98) * mm});
            skLineSegment(sketch, "E825", {"start": v(72.68, 110) * mm, "end": v(87.68, 110) * mm});
            skLineSegment(sketch, "E826", {"start": v(72.68, 130) * mm, "end": v(87.68, 130) * mm});
            skLineSegment(sketch, "E827", {"start": v(72.68, 130) * mm, "end": v(78.45, 120) * mm});
            skLineSegment(sketch, "E828", {"start": v(78.45, 120) * mm, "end": v(72.68, 110) * mm});
            skLineSegment(sketch, "E829", {"start": v(87.68, 130) * mm, "end": v(81.9, 120) * mm});
            skLineSegment(sketch, "E830", {"start": v(81.9, 120) * mm, "end": v(87.68, 110) * mm});
            skPoint(sketch, "E831", {"position": v(80.18, 131) * mm});
            skPoint(sketch, "E831.positionSnap0", {"position": v(80.18, 130) * mm});
            skPoint(sketch, "E832.positionSnap0", {"position": v(80.18, 110) * mm});
            skPoint(sketch, "E833", {"position": v(74.12, 114.5) * mm});
            skPoint(sketch, "E834", {"position": v(86.24, 114.5) * mm});
            skPoint(sketch, "E835", {"position": v(86.34, 125.67) * mm});
            skPoint(sketch, "E836", {"position": v(73.34, 126.85) * mm});
            skLineSegment(sketch, "E837", {"start": v(83.06, 120) * mm, "end": v(82.71, 120.6) * mm});
            skPoint(sketch, "E838", {"position": v(89.41, 131) * mm});
            skPoint(sketch, "E839", {"position": v(83.06, 120) * mm});
            skLineSegment(sketch, "E840", {"start": v(72.68, 132) * mm, "end": v(87.68, 132) * mm});
            skLineSegment(sketch, "E841", {"start": v(72.68, 152) * mm, "end": v(87.68, 152) * mm});
            skLineSegment(sketch, "E842", {"start": v(72.68, 152) * mm, "end": v(78.45, 142) * mm});
            skLineSegment(sketch, "E843", {"start": v(78.45, 142) * mm, "end": v(72.68, 132) * mm});
            skLineSegment(sketch, "E844", {"start": v(87.68, 152) * mm, "end": v(81.9, 142) * mm});
            skLineSegment(sketch, "E845", {"start": v(81.9, 142) * mm, "end": v(87.68, 132) * mm});
            skPoint(sketch, "E846", {"position": v(80.18, 153) * mm});
            skPoint(sketch, "E846.positionSnap0", {"position": v(80.18, 152) * mm});
            skPoint(sketch, "E847.positionSnap0", {"position": v(80.18, 132) * mm});
            skPoint(sketch, "E848", {"position": v(74.12, 136.5) * mm});
            skPoint(sketch, "E849", {"position": v(86.24, 136.5) * mm});
            skPoint(sketch, "E850", {"position": v(86.34, 147.67) * mm});
            skPoint(sketch, "E851", {"position": v(73.34, 148.85) * mm});
            skLineSegment(sketch, "E852", {"start": v(83.06, 142) * mm, "end": v(82.71, 142.6) * mm});
            skPoint(sketch, "E853", {"position": v(89.41, 153) * mm});
            skPoint(sketch, "E854", {"position": v(83.06, 142) * mm});
            skLineSegment(sketch, "E855", {"start": v(72.68, 154) * mm, "end": v(87.68, 154) * mm});
            skLineSegment(sketch, "E856", {"start": v(72.68, 174) * mm, "end": v(87.68, 174) * mm});
            skLineSegment(sketch, "E857", {"start": v(72.68, 174) * mm, "end": v(78.45, 164) * mm});
            skLineSegment(sketch, "E858", {"start": v(78.45, 164) * mm, "end": v(72.68, 154) * mm});
            skLineSegment(sketch, "E859", {"start": v(87.68, 174) * mm, "end": v(81.9, 164) * mm});
            skLineSegment(sketch, "E860", {"start": v(81.9, 164) * mm, "end": v(87.68, 154) * mm});
            skPoint(sketch, "E861", {"position": v(80.18, 175) * mm});
            skPoint(sketch, "E861.positionSnap0", {"position": v(80.18, 174) * mm});
            skPoint(sketch, "E862.positionSnap0", {"position": v(80.18, 154) * mm});
            skPoint(sketch, "E863", {"position": v(74.12, 158.5) * mm});
            skPoint(sketch, "E864", {"position": v(86.24, 158.5) * mm});
            skPoint(sketch, "E865", {"position": v(86.34, 169.67) * mm});
            skPoint(sketch, "E866", {"position": v(73.34, 170.85) * mm});
            skLineSegment(sketch, "E867", {"start": v(83.06, 164) * mm, "end": v(82.71, 164.6) * mm});
            skPoint(sketch, "E868", {"position": v(89.41, 175) * mm});
            skPoint(sketch, "E869", {"position": v(83.06, 164) * mm});
            skLineSegment(sketch, "E870", {"start": v(84.8, 11) * mm, "end": v(99.8, 11) * mm});
            skLineSegment(sketch, "E871", {"start": v(84.8, 31) * mm, "end": v(99.8, 31) * mm});
            skLineSegment(sketch, "E872", {"start": v(84.8, 31) * mm, "end": v(90.57, 21) * mm});
            skLineSegment(sketch, "E873", {"start": v(90.57, 21) * mm, "end": v(84.8, 11) * mm});
            skLineSegment(sketch, "E874", {"start": v(99.8, 31) * mm, "end": v(94.02, 21) * mm});
            skLineSegment(sketch, "E875", {"start": v(94.02, 21) * mm, "end": v(99.8, 11) * mm});
            skPoint(sketch, "E876", {"position": v(92.3, 32) * mm});
            skPoint(sketch, "E876.positionSnap0", {"position": v(92.3, 31) * mm});
            skPoint(sketch, "E877", {"position": v(92.3, 10) * mm});
            skPoint(sketch, "E877.positionSnap0", {"position": v(92.3, 11) * mm});
            skPoint(sketch, "E878", {"position": v(86.23, 15.5) * mm});
            skPoint(sketch, "E879", {"position": v(98.35, 15.5) * mm});
            skPoint(sketch, "E880", {"position": v(98.45, 26.67) * mm});
            skPoint(sketch, "E881", {"position": v(85.46, 27.85) * mm});
            skLineSegment(sketch, "E882", {"start": v(95.17, 21) * mm, "end": v(94.83, 21.6) * mm});
            skPoint(sketch, "E883", {"position": v(101.52, 32) * mm});
            skPoint(sketch, "E884", {"position": v(95.17, 21) * mm});
            skPoint(sketch, "E885", {"position": v(101.52, 10) * mm});
            skLineSegment(sketch, "E886", {"start": v(84.8, 33) * mm, "end": v(99.8, 33) * mm});
            skLineSegment(sketch, "E887", {"start": v(84.8, 53) * mm, "end": v(99.8, 53) * mm});
            skLineSegment(sketch, "E888", {"start": v(84.8, 53) * mm, "end": v(90.57, 43) * mm});
            skLineSegment(sketch, "E889", {"start": v(90.57, 43) * mm, "end": v(84.8, 33) * mm});
            skLineSegment(sketch, "E890", {"start": v(99.8, 53) * mm, "end": v(94.02, 43) * mm});
            skLineSegment(sketch, "E891", {"start": v(94.02, 43) * mm, "end": v(99.8, 33) * mm});
            skPoint(sketch, "E892", {"position": v(92.3, 54) * mm});
            skPoint(sketch, "E892.positionSnap0", {"position": v(92.3, 53) * mm});
            skPoint(sketch, "E893.positionSnap0", {"position": v(92.3, 33) * mm});
            skPoint(sketch, "E894", {"position": v(86.23, 37.5) * mm});
            skPoint(sketch, "E895", {"position": v(98.35, 37.5) * mm});
            skPoint(sketch, "E896", {"position": v(98.45, 48.67) * mm});
            skPoint(sketch, "E897", {"position": v(85.46, 49.85) * mm});
            skLineSegment(sketch, "E898", {"start": v(95.17, 43) * mm, "end": v(94.83, 43.6) * mm});
            skPoint(sketch, "E899", {"position": v(101.52, 54) * mm});
            skPoint(sketch, "E900", {"position": v(95.17, 43) * mm});
            skLineSegment(sketch, "E901", {"start": v(84.8, 55) * mm, "end": v(99.8, 55) * mm});
            skLineSegment(sketch, "E902", {"start": v(84.8, 75) * mm, "end": v(99.8, 75) * mm});
            skLineSegment(sketch, "E903", {"start": v(84.8, 75) * mm, "end": v(90.57, 65) * mm});
            skLineSegment(sketch, "E904", {"start": v(90.57, 65) * mm, "end": v(84.8, 55) * mm});
            skLineSegment(sketch, "E905", {"start": v(99.8, 75) * mm, "end": v(94.02, 65) * mm});
            skLineSegment(sketch, "E906", {"start": v(94.02, 65) * mm, "end": v(99.8, 55) * mm});
            skPoint(sketch, "E907", {"position": v(92.3, 76) * mm});
            skPoint(sketch, "E907.positionSnap0", {"position": v(92.3, 75) * mm});
            skPoint(sketch, "E908.positionSnap0", {"position": v(92.3, 55) * mm});
            skPoint(sketch, "E909", {"position": v(86.23, 59.5) * mm});
            skPoint(sketch, "E910", {"position": v(98.35, 59.5) * mm});
            skPoint(sketch, "E911", {"position": v(98.45, 70.67) * mm});
            skPoint(sketch, "E912", {"position": v(85.46, 71.85) * mm});
            skLineSegment(sketch, "E913", {"start": v(95.17, 65) * mm, "end": v(94.83, 65.6) * mm});
            skPoint(sketch, "E914", {"position": v(101.52, 76) * mm});
            skPoint(sketch, "E915", {"position": v(95.17, 65) * mm});
            skLineSegment(sketch, "E916", {"start": v(84.8, 77) * mm, "end": v(99.8, 77) * mm});
            skLineSegment(sketch, "E917", {"start": v(84.8, 97) * mm, "end": v(99.8, 97) * mm});
            skLineSegment(sketch, "E918", {"start": v(84.8, 97) * mm, "end": v(90.57, 87) * mm});
            skLineSegment(sketch, "E919", {"start": v(90.57, 87) * mm, "end": v(84.8, 77) * mm});
            skLineSegment(sketch, "E920", {"start": v(99.8, 97) * mm, "end": v(94.02, 87) * mm});
            skLineSegment(sketch, "E921", {"start": v(94.02, 87) * mm, "end": v(99.8, 77) * mm});
            skPoint(sketch, "E922", {"position": v(92.3, 98) * mm});
            skPoint(sketch, "E922.positionSnap0", {"position": v(92.3, 97) * mm});
            skPoint(sketch, "E923.positionSnap0", {"position": v(92.3, 77) * mm});
            skPoint(sketch, "E924", {"position": v(86.23, 81.5) * mm});
            skPoint(sketch, "E925", {"position": v(98.35, 81.5) * mm});
            skPoint(sketch, "E926", {"position": v(98.45, 92.67) * mm});
            skPoint(sketch, "E927", {"position": v(85.46, 93.85) * mm});
            skLineSegment(sketch, "E928", {"start": v(95.17, 87) * mm, "end": v(94.83, 87.6) * mm});
            skPoint(sketch, "E929", {"position": v(101.52, 98) * mm});
            skPoint(sketch, "E930", {"position": v(95.17, 87) * mm});
            skLineSegment(sketch, "E931", {"start": v(84.8, 99) * mm, "end": v(99.8, 99) * mm});
            skLineSegment(sketch, "E932", {"start": v(84.8, 119) * mm, "end": v(99.8, 119) * mm});
            skLineSegment(sketch, "E933", {"start": v(84.8, 119) * mm, "end": v(90.57, 109) * mm});
            skLineSegment(sketch, "E934", {"start": v(90.57, 109) * mm, "end": v(84.8, 99) * mm});
            skLineSegment(sketch, "E935", {"start": v(99.8, 119) * mm, "end": v(94.02, 109) * mm});
            skLineSegment(sketch, "E936", {"start": v(94.02, 109) * mm, "end": v(99.8, 99) * mm});
            skPoint(sketch, "E937", {"position": v(92.3, 120) * mm});
            skPoint(sketch, "E937.positionSnap0", {"position": v(92.3, 119) * mm});
            skPoint(sketch, "E938.positionSnap0", {"position": v(92.3, 99) * mm});
            skPoint(sketch, "E939", {"position": v(86.23, 103.5) * mm});
            skPoint(sketch, "E940", {"position": v(98.35, 103.5) * mm});
            skPoint(sketch, "E941", {"position": v(98.45, 114.67) * mm});
            skPoint(sketch, "E942", {"position": v(85.46, 115.85) * mm});
            skLineSegment(sketch, "E943", {"start": v(95.17, 109) * mm, "end": v(94.83, 109.6) * mm});
            skPoint(sketch, "E944", {"position": v(101.52, 120) * mm});
            skPoint(sketch, "E945", {"position": v(95.17, 109) * mm});
            skLineSegment(sketch, "E946", {"start": v(84.8, 121) * mm, "end": v(99.8, 121) * mm});
            skLineSegment(sketch, "E947", {"start": v(84.8, 141) * mm, "end": v(99.8, 141) * mm});
            skLineSegment(sketch, "E948", {"start": v(84.8, 141) * mm, "end": v(90.57, 131) * mm});
            skLineSegment(sketch, "E949", {"start": v(90.57, 131) * mm, "end": v(84.8, 121) * mm});
            skLineSegment(sketch, "E950", {"start": v(99.8, 141) * mm, "end": v(94.02, 131) * mm});
            skLineSegment(sketch, "E951", {"start": v(94.02, 131) * mm, "end": v(99.8, 121) * mm});
            skPoint(sketch, "E952", {"position": v(92.3, 142) * mm});
            skPoint(sketch, "E952.positionSnap0", {"position": v(92.3, 141) * mm});
            skPoint(sketch, "E953.positionSnap0", {"position": v(92.3, 121) * mm});
            skPoint(sketch, "E954", {"position": v(86.23, 125.5) * mm});
            skPoint(sketch, "E955", {"position": v(98.35, 125.5) * mm});
            skPoint(sketch, "E956", {"position": v(98.45, 136.67) * mm});
            skPoint(sketch, "E957", {"position": v(85.46, 137.85) * mm});
            skLineSegment(sketch, "E958", {"start": v(95.17, 131) * mm, "end": v(94.83, 131.6) * mm});
            skPoint(sketch, "E959", {"position": v(101.52, 142) * mm});
            skPoint(sketch, "E960", {"position": v(95.17, 131) * mm});
            skLineSegment(sketch, "E961", {"start": v(84.8, 143) * mm, "end": v(99.8, 143) * mm});
            skLineSegment(sketch, "E962", {"start": v(84.8, 163) * mm, "end": v(99.8, 163) * mm});
            skLineSegment(sketch, "E963", {"start": v(84.8, 163) * mm, "end": v(90.57, 153) * mm});
            skLineSegment(sketch, "E964", {"start": v(90.57, 153) * mm, "end": v(84.8, 143) * mm});
            skLineSegment(sketch, "E965", {"start": v(99.8, 163) * mm, "end": v(94.02, 153) * mm});
            skLineSegment(sketch, "E966", {"start": v(94.02, 153) * mm, "end": v(99.8, 143) * mm});
            skPoint(sketch, "E967", {"position": v(92.3, 164) * mm});
            skPoint(sketch, "E967.positionSnap0", {"position": v(92.3, 163) * mm});
            skPoint(sketch, "E968.positionSnap0", {"position": v(92.3, 143) * mm});
            skPoint(sketch, "E969", {"position": v(86.23, 147.5) * mm});
            skPoint(sketch, "E970", {"position": v(98.35, 147.5) * mm});
            skPoint(sketch, "E971", {"position": v(98.45, 158.67) * mm});
            skPoint(sketch, "E972", {"position": v(85.46, 159.85) * mm});
            skLineSegment(sketch, "E973", {"start": v(95.17, 153) * mm, "end": v(94.83, 153.6) * mm});
            skPoint(sketch, "E974", {"position": v(101.52, 164) * mm});
            skPoint(sketch, "E975", {"position": v(95.17, 153) * mm});
            skLineSegment(sketch, "E976", {"start": v(84.8, 165) * mm, "end": v(99.8, 165) * mm});
            skLineSegment(sketch, "E977", {"start": v(84.8, 185) * mm, "end": v(99.8, 185) * mm});
            skLineSegment(sketch, "E978", {"start": v(84.8, 185) * mm, "end": v(90.57, 175) * mm});
            skLineSegment(sketch, "E979", {"start": v(90.57, 175) * mm, "end": v(84.8, 165) * mm});
            skLineSegment(sketch, "E980", {"start": v(99.8, 185) * mm, "end": v(94.02, 175) * mm});
            skLineSegment(sketch, "E981", {"start": v(94.02, 175) * mm, "end": v(99.8, 165) * mm});
            skPoint(sketch, "E982", {"position": v(92.3, 186) * mm});
            skPoint(sketch, "E982.positionSnap0", {"position": v(92.3, 185) * mm});
            skPoint(sketch, "E983.positionSnap0", {"position": v(92.3, 165) * mm});
            skPoint(sketch, "E984", {"position": v(86.23, 169.5) * mm});
            skPoint(sketch, "E985", {"position": v(98.35, 169.5) * mm});
            skPoint(sketch, "E986", {"position": v(98.45, 180.67) * mm});
            skPoint(sketch, "E987", {"position": v(85.46, 181.85) * mm});
            skLineSegment(sketch, "E988", {"start": v(95.17, 175) * mm, "end": v(94.83, 175.6) * mm});
            skPoint(sketch, "E989", {"position": v(83.06, 186) * mm});
            skPoint(sketch, "E990", {"position": v(101.52, 186) * mm});
            skPoint(sketch, "E991", {"position": v(95.17, 175) * mm});
            skLineSegment(sketch, "E992", {"start": v(96.9, 0) * mm, "end": v(111.9, 0) * mm});
            skLineSegment(sketch, "E993", {"start": v(96.9, 20) * mm, "end": v(111.9, 20) * mm});
            skLineSegment(sketch, "E994", {"start": v(96.9, 20) * mm, "end": v(102.68, 10) * mm});
            skLineSegment(sketch, "E995", {"start": v(102.68, 10) * mm, "end": v(96.9, 0) * mm});
            skLineSegment(sketch, "E996", {"start": v(111.9, 20) * mm, "end": v(106.13, 10) * mm});
            skLineSegment(sketch, "E997", {"start": v(106.13, 10) * mm, "end": v(111.9, 0) * mm});
            skPoint(sketch, "E998", {"position": v(104.4, 21) * mm});
            skPoint(sketch, "E998.positionSnap0", {"position": v(104.4, 20) * mm});
            skPoint(sketch, "E999", {"position": v(104.4, -1) * mm});
            skPoint(sketch, "E999.positionSnap0", {"position": v(104.4, 0) * mm});
            skPoint(sketch, "E1000", {"position": v(98.35, 4.5) * mm});
            skPoint(sketch, "E1001", {"position": v(110.47, 4.5) * mm});
            skPoint(sketch, "E1002", {"position": v(110.56, 15.67) * mm});
            skPoint(sketch, "E1003", {"position": v(97.57, 16.85) * mm});
            skLineSegment(sketch, "E1004", {"start": v(107.29, 10) * mm, "end": v(106.94, 10.6) * mm});
            skPoint(sketch, "E1005", {"position": v(113.64, 21) * mm});
            skPoint(sketch, "E1006", {"position": v(107.29, 10) * mm});
            skPoint(sketch, "E1007", {"position": v(95.17, -1) * mm});
            skPoint(sketch, "E1008", {"position": v(113.64, -1) * mm});
            skLineSegment(sketch, "E1009", {"start": v(96.9, 22) * mm, "end": v(111.9, 22) * mm});
            skLineSegment(sketch, "E1010", {"start": v(96.9, 42) * mm, "end": v(111.9, 42) * mm});
            skLineSegment(sketch, "E1011", {"start": v(96.9, 42) * mm, "end": v(102.68, 32) * mm});
            skLineSegment(sketch, "E1012", {"start": v(102.68, 32) * mm, "end": v(96.9, 22) * mm});
            skLineSegment(sketch, "E1013", {"start": v(111.9, 42) * mm, "end": v(106.13, 32) * mm});
            skLineSegment(sketch, "E1014", {"start": v(106.13, 32) * mm, "end": v(111.9, 22) * mm});
            skPoint(sketch, "E1015", {"position": v(104.4, 43) * mm});
            skPoint(sketch, "E1015.positionSnap0", {"position": v(104.4, 42) * mm});
            skPoint(sketch, "E1016.positionSnap0", {"position": v(104.4, 22) * mm});
            skPoint(sketch, "E1017", {"position": v(98.35, 26.5) * mm});
            skPoint(sketch, "E1018", {"position": v(110.47, 26.5) * mm});
            skPoint(sketch, "E1019", {"position": v(110.56, 37.67) * mm});
            skPoint(sketch, "E1020", {"position": v(97.57, 38.85) * mm});
            skLineSegment(sketch, "E1021", {"start": v(107.29, 32) * mm, "end": v(106.94, 32.6) * mm});
            skPoint(sketch, "E1022", {"position": v(113.64, 43) * mm});
            skPoint(sketch, "E1023", {"position": v(107.29, 32) * mm});
            skLineSegment(sketch, "E1024", {"start": v(96.9, 44) * mm, "end": v(111.9, 44) * mm});
            skLineSegment(sketch, "E1025", {"start": v(96.9, 64) * mm, "end": v(111.9, 64) * mm});
            skLineSegment(sketch, "E1026", {"start": v(96.9, 64) * mm, "end": v(102.68, 54) * mm});
            skLineSegment(sketch, "E1027", {"start": v(102.68, 54) * mm, "end": v(96.9, 44) * mm});
            skLineSegment(sketch, "E1028", {"start": v(111.9, 64) * mm, "end": v(106.13, 54) * mm});
            skLineSegment(sketch, "E1029", {"start": v(106.13, 54) * mm, "end": v(111.9, 44) * mm});
            skPoint(sketch, "E1030", {"position": v(104.4, 65) * mm});
            skPoint(sketch, "E1030.positionSnap0", {"position": v(104.4, 64) * mm});
            skPoint(sketch, "E1031.positionSnap0", {"position": v(104.4, 44) * mm});
            skPoint(sketch, "E1032", {"position": v(98.35, 48.5) * mm});
            skPoint(sketch, "E1033", {"position": v(110.47, 48.5) * mm});
            skPoint(sketch, "E1034", {"position": v(110.56, 59.67) * mm});
            skPoint(sketch, "E1035", {"position": v(97.57, 60.85) * mm});
            skLineSegment(sketch, "E1036", {"start": v(107.29, 54) * mm, "end": v(106.94, 54.6) * mm});
            skPoint(sketch, "E1037", {"position": v(113.64, 65) * mm});
            skPoint(sketch, "E1038", {"position": v(107.29, 54) * mm});
            skLineSegment(sketch, "E1039", {"start": v(96.9, 66) * mm, "end": v(111.9, 66) * mm});
            skLineSegment(sketch, "E1040", {"start": v(96.9, 86) * mm, "end": v(111.9, 86) * mm});
            skLineSegment(sketch, "E1041", {"start": v(96.9, 86) * mm, "end": v(102.68, 76) * mm});
            skLineSegment(sketch, "E1042", {"start": v(102.68, 76) * mm, "end": v(96.9, 66) * mm});
            skLineSegment(sketch, "E1043", {"start": v(111.9, 86) * mm, "end": v(106.13, 76) * mm});
            skLineSegment(sketch, "E1044", {"start": v(106.13, 76) * mm, "end": v(111.9, 66) * mm});
            skPoint(sketch, "E1045", {"position": v(104.4, 87) * mm});
            skPoint(sketch, "E1045.positionSnap0", {"position": v(104.4, 86) * mm});
            skPoint(sketch, "E1046.positionSnap0", {"position": v(104.4, 66) * mm});
            skPoint(sketch, "E1047", {"position": v(98.35, 70.5) * mm});
            skPoint(sketch, "E1048", {"position": v(110.47, 70.5) * mm});
            skPoint(sketch, "E1049", {"position": v(110.56, 81.67) * mm});
            skPoint(sketch, "E1050", {"position": v(97.57, 82.85) * mm});
            skLineSegment(sketch, "E1051", {"start": v(107.29, 76) * mm, "end": v(106.94, 76.6) * mm});
            skPoint(sketch, "E1052", {"position": v(113.64, 87) * mm});
            skPoint(sketch, "E1053", {"position": v(107.29, 76) * mm});
            skLineSegment(sketch, "E1054", {"start": v(96.9, 88) * mm, "end": v(111.9, 88) * mm});
            skLineSegment(sketch, "E1055", {"start": v(96.9, 108) * mm, "end": v(111.9, 108) * mm});
            skLineSegment(sketch, "E1056", {"start": v(96.9, 108) * mm, "end": v(102.68, 98) * mm});
            skLineSegment(sketch, "E1057", {"start": v(102.68, 98) * mm, "end": v(96.9, 88) * mm});
            skLineSegment(sketch, "E1058", {"start": v(111.9, 108) * mm, "end": v(106.13, 98) * mm});
            skLineSegment(sketch, "E1059", {"start": v(106.13, 98) * mm, "end": v(111.9, 88) * mm});
            skPoint(sketch, "E1060", {"position": v(104.4, 109) * mm});
            skPoint(sketch, "E1060.positionSnap0", {"position": v(104.4, 108) * mm});
            skPoint(sketch, "E1061.positionSnap0", {"position": v(104.4, 88) * mm});
            skPoint(sketch, "E1062", {"position": v(98.35, 92.5) * mm});
            skPoint(sketch, "E1063", {"position": v(110.47, 92.5) * mm});
            skPoint(sketch, "E1064", {"position": v(110.56, 103.67) * mm});
            skPoint(sketch, "E1065", {"position": v(97.57, 104.85) * mm});
            skLineSegment(sketch, "E1066", {"start": v(107.29, 98) * mm, "end": v(106.94, 98.6) * mm});
            skPoint(sketch, "E1067", {"position": v(113.64, 109) * mm});
            skPoint(sketch, "E1068", {"position": v(107.29, 98) * mm});
            skLineSegment(sketch, "E1069", {"start": v(96.9, 110) * mm, "end": v(111.9, 110) * mm});
            skLineSegment(sketch, "E1070", {"start": v(96.9, 130) * mm, "end": v(111.9, 130) * mm});
            skLineSegment(sketch, "E1071", {"start": v(96.9, 130) * mm, "end": v(102.68, 120) * mm});
            skLineSegment(sketch, "E1072", {"start": v(102.68, 120) * mm, "end": v(96.9, 110) * mm});
            skLineSegment(sketch, "E1073", {"start": v(111.9, 130) * mm, "end": v(106.13, 120) * mm});
            skLineSegment(sketch, "E1074", {"start": v(106.13, 120) * mm, "end": v(111.9, 110) * mm});
            skPoint(sketch, "E1075", {"position": v(104.4, 131) * mm});
            skPoint(sketch, "E1075.positionSnap0", {"position": v(104.4, 130) * mm});
            skPoint(sketch, "E1076.positionSnap0", {"position": v(104.4, 110) * mm});
            skPoint(sketch, "E1077", {"position": v(98.35, 114.5) * mm});
            skPoint(sketch, "E1078", {"position": v(110.47, 114.5) * mm});
            skPoint(sketch, "E1079", {"position": v(110.56, 125.67) * mm});
            skPoint(sketch, "E1080", {"position": v(97.57, 126.85) * mm});
            skLineSegment(sketch, "E1081", {"start": v(107.29, 120) * mm, "end": v(106.94, 120.6) * mm});
            skPoint(sketch, "E1082", {"position": v(113.64, 131) * mm});
            skPoint(sketch, "E1083", {"position": v(107.29, 120) * mm});
            skLineSegment(sketch, "E1084", {"start": v(96.9, 132) * mm, "end": v(111.9, 132) * mm});
            skLineSegment(sketch, "E1085", {"start": v(96.9, 152) * mm, "end": v(111.9, 152) * mm});
            skLineSegment(sketch, "E1086", {"start": v(96.9, 152) * mm, "end": v(102.68, 142) * mm});
            skLineSegment(sketch, "E1087", {"start": v(102.68, 142) * mm, "end": v(96.9, 132) * mm});
            skLineSegment(sketch, "E1088", {"start": v(111.9, 152) * mm, "end": v(106.13, 142) * mm});
            skLineSegment(sketch, "E1089", {"start": v(106.13, 142) * mm, "end": v(111.9, 132) * mm});
            skPoint(sketch, "E1090", {"position": v(104.4, 153) * mm});
            skPoint(sketch, "E1090.positionSnap0", {"position": v(104.4, 152) * mm});
            skPoint(sketch, "E1091.positionSnap0", {"position": v(104.4, 132) * mm});
            skPoint(sketch, "E1092", {"position": v(98.35, 136.5) * mm});
            skPoint(sketch, "E1093", {"position": v(110.47, 136.5) * mm});
            skPoint(sketch, "E1094", {"position": v(110.56, 147.67) * mm});
            skPoint(sketch, "E1095", {"position": v(97.57, 148.85) * mm});
            skLineSegment(sketch, "E1096", {"start": v(107.29, 142) * mm, "end": v(106.94, 142.6) * mm});
            skPoint(sketch, "E1097", {"position": v(113.64, 153) * mm});
            skPoint(sketch, "E1098", {"position": v(107.29, 142) * mm});
            skLineSegment(sketch, "E1099", {"start": v(96.9, 154) * mm, "end": v(111.9, 154) * mm});
            skLineSegment(sketch, "E1100", {"start": v(96.9, 174) * mm, "end": v(111.9, 174) * mm});
            skLineSegment(sketch, "E1101", {"start": v(96.9, 174) * mm, "end": v(102.68, 164) * mm});
            skLineSegment(sketch, "E1102", {"start": v(102.68, 164) * mm, "end": v(96.9, 154) * mm});
            skLineSegment(sketch, "E1103", {"start": v(111.9, 174) * mm, "end": v(106.13, 164) * mm});
            skLineSegment(sketch, "E1104", {"start": v(106.13, 164) * mm, "end": v(111.9, 154) * mm});
            skPoint(sketch, "E1105", {"position": v(104.4, 175) * mm});
            skPoint(sketch, "E1105.positionSnap0", {"position": v(104.4, 174) * mm});
            skPoint(sketch, "E1106.positionSnap0", {"position": v(104.4, 154) * mm});
            skPoint(sketch, "E1107", {"position": v(98.35, 158.5) * mm});
            skPoint(sketch, "E1108", {"position": v(110.47, 158.5) * mm});
            skPoint(sketch, "E1109", {"position": v(110.56, 169.67) * mm});
            skPoint(sketch, "E1110", {"position": v(97.57, 170.85) * mm});
            skLineSegment(sketch, "E1111", {"start": v(107.29, 164) * mm, "end": v(106.94, 164.6) * mm});
            skPoint(sketch, "E1112", {"position": v(113.64, 175) * mm});
            skPoint(sketch, "E1113", {"position": v(107.29, 164) * mm});
            skLineSegment(sketch, "E1114", {"start": v(109.02, 11) * mm, "end": v(124.02, 11) * mm});
            skLineSegment(sketch, "E1115", {"start": v(109.02, 31) * mm, "end": v(124.02, 31) * mm});
            skLineSegment(sketch, "E1116", {"start": v(109.02, 31) * mm, "end": v(114.8, 21) * mm});
            skLineSegment(sketch, "E1117", {"start": v(114.8, 21) * mm, "end": v(109.02, 11) * mm});
            skLineSegment(sketch, "E1118", {"start": v(124.02, 31) * mm, "end": v(118.25, 21) * mm});
            skLineSegment(sketch, "E1119", {"start": v(118.25, 21) * mm, "end": v(124.02, 11) * mm});
            skPoint(sketch, "E1120", {"position": v(116.52, 32) * mm});
            skPoint(sketch, "E1120.positionSnap0", {"position": v(116.52, 31) * mm});
            skPoint(sketch, "E1121", {"position": v(116.52, 10) * mm});
            skPoint(sketch, "E1121.positionSnap0", {"position": v(116.52, 11) * mm});
            skPoint(sketch, "E1122", {"position": v(110.46, 15.5) * mm});
            skPoint(sketch, "E1123", {"position": v(122.58, 15.5) * mm});
            skPoint(sketch, "E1124", {"position": v(122.68, 26.67) * mm});
            skPoint(sketch, "E1125", {"position": v(109.68, 27.85) * mm});
            skLineSegment(sketch, "E1126", {"start": v(119.4, 21) * mm, "end": v(119.05, 21.6) * mm});
            skPoint(sketch, "E1127", {"position": v(125.75, 32) * mm});
            skPoint(sketch, "E1128", {"position": v(119.4, 21) * mm});
            skPoint(sketch, "E1129", {"position": v(125.75, 10) * mm});
            skLineSegment(sketch, "E1130", {"start": v(109.02, 33) * mm, "end": v(124.02, 33) * mm});
            skLineSegment(sketch, "E1131", {"start": v(109.02, 53) * mm, "end": v(124.02, 53) * mm});
            skLineSegment(sketch, "E1132", {"start": v(109.02, 53) * mm, "end": v(114.8, 43) * mm});
            skLineSegment(sketch, "E1133", {"start": v(114.8, 43) * mm, "end": v(109.02, 33) * mm});
            skLineSegment(sketch, "E1134", {"start": v(124.02, 53) * mm, "end": v(118.25, 43) * mm});
            skLineSegment(sketch, "E1135", {"start": v(118.25, 43) * mm, "end": v(124.02, 33) * mm});
            skPoint(sketch, "E1136", {"position": v(116.52, 54) * mm});
            skPoint(sketch, "E1136.positionSnap0", {"position": v(116.52, 53) * mm});
            skPoint(sketch, "E1137.positionSnap0", {"position": v(116.52, 33) * mm});
            skPoint(sketch, "E1138", {"position": v(110.46, 37.5) * mm});
            skPoint(sketch, "E1139", {"position": v(122.58, 37.5) * mm});
            skPoint(sketch, "E1140", {"position": v(122.68, 48.67) * mm});
            skPoint(sketch, "E1141", {"position": v(109.68, 49.85) * mm});
            skLineSegment(sketch, "E1142", {"start": v(119.4, 43) * mm, "end": v(119.05, 43.6) * mm});
            skPoint(sketch, "E1143", {"position": v(125.75, 54) * mm});
            skPoint(sketch, "E1144", {"position": v(119.4, 43) * mm});
            skLineSegment(sketch, "E1145", {"start": v(109.02, 55) * mm, "end": v(124.02, 55) * mm});
            skLineSegment(sketch, "E1146", {"start": v(109.02, 75) * mm, "end": v(124.02, 75) * mm});
            skLineSegment(sketch, "E1147", {"start": v(109.02, 75) * mm, "end": v(114.8, 65) * mm});
            skLineSegment(sketch, "E1148", {"start": v(114.8, 65) * mm, "end": v(109.02, 55) * mm});
            skLineSegment(sketch, "E1149", {"start": v(124.02, 75) * mm, "end": v(118.25, 65) * mm});
            skLineSegment(sketch, "E1150", {"start": v(118.25, 65) * mm, "end": v(124.02, 55) * mm});
            skPoint(sketch, "E1151", {"position": v(116.52, 76) * mm});
            skPoint(sketch, "E1151.positionSnap0", {"position": v(116.52, 75) * mm});
            skPoint(sketch, "E1152.positionSnap0", {"position": v(116.52, 55) * mm});
            skPoint(sketch, "E1153", {"position": v(110.46, 59.5) * mm});
            skPoint(sketch, "E1154", {"position": v(122.58, 59.5) * mm});
            skPoint(sketch, "E1155", {"position": v(122.68, 70.67) * mm});
            skPoint(sketch, "E1156", {"position": v(109.68, 71.85) * mm});
            skLineSegment(sketch, "E1157", {"start": v(119.4, 65) * mm, "end": v(119.05, 65.6) * mm});
            skPoint(sketch, "E1158", {"position": v(125.75, 76) * mm});
            skPoint(sketch, "E1159", {"position": v(119.4, 65) * mm});
            skLineSegment(sketch, "E1160", {"start": v(109.02, 77) * mm, "end": v(124.02, 77) * mm});
            skLineSegment(sketch, "E1161", {"start": v(109.02, 97) * mm, "end": v(124.02, 97) * mm});
            skLineSegment(sketch, "E1162", {"start": v(109.02, 97) * mm, "end": v(114.8, 87) * mm});
            skLineSegment(sketch, "E1163", {"start": v(114.8, 87) * mm, "end": v(109.02, 77) * mm});
            skLineSegment(sketch, "E1164", {"start": v(124.02, 97) * mm, "end": v(118.25, 87) * mm});
            skLineSegment(sketch, "E1165", {"start": v(118.25, 87) * mm, "end": v(124.02, 77) * mm});
            skPoint(sketch, "E1166", {"position": v(116.52, 98) * mm});
            skPoint(sketch, "E1166.positionSnap0", {"position": v(116.52, 97) * mm});
            skPoint(sketch, "E1167.positionSnap0", {"position": v(116.52, 77) * mm});
            skPoint(sketch, "E1168", {"position": v(110.46, 81.5) * mm});
            skPoint(sketch, "E1169", {"position": v(122.58, 81.5) * mm});
            skPoint(sketch, "E1170", {"position": v(122.68, 92.67) * mm});
            skPoint(sketch, "E1171", {"position": v(109.68, 93.85) * mm});
            skLineSegment(sketch, "E1172", {"start": v(119.4, 87) * mm, "end": v(119.05, 87.6) * mm});
            skPoint(sketch, "E1173", {"position": v(125.75, 98) * mm});
            skPoint(sketch, "E1174", {"position": v(119.4, 87) * mm});
            skLineSegment(sketch, "E1175", {"start": v(109.02, 99) * mm, "end": v(124.02, 99) * mm});
            skLineSegment(sketch, "E1176", {"start": v(109.02, 119) * mm, "end": v(124.02, 119) * mm});
            skLineSegment(sketch, "E1177", {"start": v(109.02, 119) * mm, "end": v(114.8, 109) * mm});
            skLineSegment(sketch, "E1178", {"start": v(114.8, 109) * mm, "end": v(109.02, 99) * mm});
            skLineSegment(sketch, "E1179", {"start": v(124.02, 119) * mm, "end": v(118.25, 109) * mm});
            skLineSegment(sketch, "E1180", {"start": v(118.25, 109) * mm, "end": v(124.02, 99) * mm});
            skPoint(sketch, "E1181", {"position": v(116.52, 120) * mm});
            skPoint(sketch, "E1181.positionSnap0", {"position": v(116.52, 119) * mm});
            skPoint(sketch, "E1182.positionSnap0", {"position": v(116.52, 99) * mm});
            skPoint(sketch, "E1183", {"position": v(110.46, 103.5) * mm});
            skPoint(sketch, "E1184", {"position": v(122.58, 103.5) * mm});
            skPoint(sketch, "E1185", {"position": v(122.68, 114.67) * mm});
            skPoint(sketch, "E1186", {"position": v(109.68, 115.85) * mm});
            skLineSegment(sketch, "E1187", {"start": v(119.4, 109) * mm, "end": v(119.05, 109.6) * mm});
            skPoint(sketch, "E1188", {"position": v(125.75, 120) * mm});
            skPoint(sketch, "E1189", {"position": v(119.4, 109) * mm});
            skLineSegment(sketch, "E1190", {"start": v(109.02, 121) * mm, "end": v(124.02, 121) * mm});
            skLineSegment(sketch, "E1191", {"start": v(109.02, 141) * mm, "end": v(124.02, 141) * mm});
            skLineSegment(sketch, "E1192", {"start": v(109.02, 141) * mm, "end": v(114.8, 131) * mm});
            skLineSegment(sketch, "E1193", {"start": v(114.8, 131) * mm, "end": v(109.02, 121) * mm});
            skLineSegment(sketch, "E1194", {"start": v(124.02, 141) * mm, "end": v(118.25, 131) * mm});
            skLineSegment(sketch, "E1195", {"start": v(118.25, 131) * mm, "end": v(124.02, 121) * mm});
            skPoint(sketch, "E1196", {"position": v(116.52, 142) * mm});
            skPoint(sketch, "E1196.positionSnap0", {"position": v(116.52, 141) * mm});
            skPoint(sketch, "E1197.positionSnap0", {"position": v(116.52, 121) * mm});
            skPoint(sketch, "E1198", {"position": v(110.46, 125.5) * mm});
            skPoint(sketch, "E1199", {"position": v(122.58, 125.5) * mm});
            skPoint(sketch, "E1200", {"position": v(122.68, 136.67) * mm});
            skPoint(sketch, "E1201", {"position": v(109.68, 137.85) * mm});
            skLineSegment(sketch, "E1202", {"start": v(119.4, 131) * mm, "end": v(119.05, 131.6) * mm});
            skPoint(sketch, "E1203", {"position": v(125.75, 142) * mm});
            skPoint(sketch, "E1204", {"position": v(119.4, 131) * mm});
            skLineSegment(sketch, "E1205", {"start": v(109.02, 143) * mm, "end": v(124.02, 143) * mm});
            skLineSegment(sketch, "E1206", {"start": v(109.02, 163) * mm, "end": v(124.02, 163) * mm});
            skLineSegment(sketch, "E1207", {"start": v(109.02, 163) * mm, "end": v(114.8, 153) * mm});
            skLineSegment(sketch, "E1208", {"start": v(114.8, 153) * mm, "end": v(109.02, 143) * mm});
            skLineSegment(sketch, "E1209", {"start": v(124.02, 163) * mm, "end": v(118.25, 153) * mm});
            skLineSegment(sketch, "E1210", {"start": v(118.25, 153) * mm, "end": v(124.02, 143) * mm});
            skPoint(sketch, "E1211", {"position": v(116.52, 164) * mm});
            skPoint(sketch, "E1211.positionSnap0", {"position": v(116.52, 163) * mm});
            skPoint(sketch, "E1212.positionSnap0", {"position": v(116.52, 143) * mm});
            skPoint(sketch, "E1213", {"position": v(110.46, 147.5) * mm});
            skPoint(sketch, "E1214", {"position": v(122.58, 147.5) * mm});
            skPoint(sketch, "E1215", {"position": v(122.68, 158.67) * mm});
            skPoint(sketch, "E1216", {"position": v(109.68, 159.85) * mm});
            skLineSegment(sketch, "E1217", {"start": v(119.4, 153) * mm, "end": v(119.05, 153.6) * mm});
            skPoint(sketch, "E1218", {"position": v(125.75, 164) * mm});
            skPoint(sketch, "E1219", {"position": v(119.4, 153) * mm});
            skLineSegment(sketch, "E1220", {"start": v(109.02, 165) * mm, "end": v(124.02, 165) * mm});
            skLineSegment(sketch, "E1221", {"start": v(109.02, 185) * mm, "end": v(124.02, 185) * mm});
            skLineSegment(sketch, "E1222", {"start": v(109.02, 185) * mm, "end": v(114.8, 175) * mm});
            skLineSegment(sketch, "E1223", {"start": v(114.8, 175) * mm, "end": v(109.02, 165) * mm});
            skLineSegment(sketch, "E1224", {"start": v(124.02, 185) * mm, "end": v(118.25, 175) * mm});
            skLineSegment(sketch, "E1225", {"start": v(118.25, 175) * mm, "end": v(124.02, 165) * mm});
            skPoint(sketch, "E1226", {"position": v(116.52, 186) * mm});
            skPoint(sketch, "E1226.positionSnap0", {"position": v(116.52, 185) * mm});
            skPoint(sketch, "E1227.positionSnap0", {"position": v(116.52, 165) * mm});
            skPoint(sketch, "E1228", {"position": v(110.46, 169.5) * mm});
            skPoint(sketch, "E1229", {"position": v(122.58, 169.5) * mm});
            skPoint(sketch, "E1230", {"position": v(122.68, 180.67) * mm});
            skPoint(sketch, "E1231", {"position": v(109.68, 181.85) * mm});
            skLineSegment(sketch, "E1232", {"start": v(119.4, 175) * mm, "end": v(119.05, 175.6) * mm});
            skPoint(sketch, "E1233", {"position": v(107.29, 186) * mm});
            skPoint(sketch, "E1234", {"position": v(125.75, 186) * mm});
            skPoint(sketch, "E1235", {"position": v(119.4, 175) * mm});
            skLineSegment(sketch, "E1236", {"start": v(121.13, 0) * mm, "end": v(136.13, 0) * mm});
            skLineSegment(sketch, "E1237", {"start": v(121.13, 20) * mm, "end": v(136.13, 20) * mm});
            skLineSegment(sketch, "E1238", {"start": v(121.13, 20) * mm, "end": v(126.9, 10) * mm});
            skLineSegment(sketch, "E1239", {"start": v(126.9, 10) * mm, "end": v(121.13, 0) * mm});
            skLineSegment(sketch, "E1240", {"start": v(136.13, 20) * mm, "end": v(130.36, 10) * mm});
            skLineSegment(sketch, "E1241", {"start": v(130.36, 10) * mm, "end": v(136.13, 0) * mm});
            skPoint(sketch, "E1242", {"position": v(128.63, 21) * mm});
            skPoint(sketch, "E1242.positionSnap0", {"position": v(128.63, 20) * mm});
            skPoint(sketch, "E1243", {"position": v(128.63, -1) * mm});
            skPoint(sketch, "E1243.positionSnap0", {"position": v(128.63, 0) * mm});
            skPoint(sketch, "E1244", {"position": v(122.57, 4.5) * mm});
            skPoint(sketch, "E1245", {"position": v(134.7, 4.5) * mm});
            skPoint(sketch, "E1246", {"position": v(134.79, 15.67) * mm});
            skPoint(sketch, "E1247", {"position": v(121.8, 16.85) * mm});
            skLineSegment(sketch, "E1248", {"start": v(131.51, 10) * mm, "end": v(131.17, 10.6) * mm});
            skPoint(sketch, "E1249", {"position": v(137.86, 21) * mm});
            skPoint(sketch, "E1250", {"position": v(131.51, 10) * mm});
            skPoint(sketch, "E1251", {"position": v(119.4, -1) * mm});
            skPoint(sketch, "E1252", {"position": v(137.86, -1) * mm});
            skLineSegment(sketch, "E1253", {"start": v(121.13, 22) * mm, "end": v(136.13, 22) * mm});
            skLineSegment(sketch, "E1254", {"start": v(121.13, 42) * mm, "end": v(136.13, 42) * mm});
            skLineSegment(sketch, "E1255", {"start": v(121.13, 42) * mm, "end": v(126.9, 32) * mm});
            skLineSegment(sketch, "E1256", {"start": v(126.9, 32) * mm, "end": v(121.13, 22) * mm});
            skLineSegment(sketch, "E1257", {"start": v(136.13, 42) * mm, "end": v(130.36, 32) * mm});
            skLineSegment(sketch, "E1258", {"start": v(130.36, 32) * mm, "end": v(136.13, 22) * mm});
            skPoint(sketch, "E1259", {"position": v(128.63, 43) * mm});
            skPoint(sketch, "E1259.positionSnap0", {"position": v(128.63, 42) * mm});
            skPoint(sketch, "E1260.positionSnap0", {"position": v(128.63, 22) * mm});
            skPoint(sketch, "E1261", {"position": v(122.57, 26.5) * mm});
            skPoint(sketch, "E1262", {"position": v(134.7, 26.5) * mm});
            skPoint(sketch, "E1263", {"position": v(134.79, 37.67) * mm});
            skPoint(sketch, "E1264", {"position": v(121.8, 38.85) * mm});
            skLineSegment(sketch, "E1265", {"start": v(131.51, 32) * mm, "end": v(131.17, 32.6) * mm});
            skPoint(sketch, "E1266", {"position": v(137.86, 43) * mm});
            skPoint(sketch, "E1267", {"position": v(131.51, 32) * mm});
            skLineSegment(sketch, "E1268", {"start": v(121.13, 44) * mm, "end": v(136.13, 44) * mm});
            skLineSegment(sketch, "E1269", {"start": v(121.13, 64) * mm, "end": v(136.13, 64) * mm});
            skLineSegment(sketch, "E1270", {"start": v(121.13, 64) * mm, "end": v(126.9, 54) * mm});
            skLineSegment(sketch, "E1271", {"start": v(126.9, 54) * mm, "end": v(121.13, 44) * mm});
            skLineSegment(sketch, "E1272", {"start": v(136.13, 64) * mm, "end": v(130.36, 54) * mm});
            skLineSegment(sketch, "E1273", {"start": v(130.36, 54) * mm, "end": v(136.13, 44) * mm});
            skPoint(sketch, "E1274", {"position": v(128.63, 65) * mm});
            skPoint(sketch, "E1274.positionSnap0", {"position": v(128.63, 64) * mm});
            skPoint(sketch, "E1275.positionSnap0", {"position": v(128.63, 44) * mm});
            skPoint(sketch, "E1276", {"position": v(122.57, 48.5) * mm});
            skPoint(sketch, "E1277", {"position": v(134.7, 48.5) * mm});
            skPoint(sketch, "E1278", {"position": v(134.79, 59.67) * mm});
            skPoint(sketch, "E1279", {"position": v(121.8, 60.85) * mm});
            skLineSegment(sketch, "E1280", {"start": v(131.51, 54) * mm, "end": v(131.17, 54.6) * mm});
            skPoint(sketch, "E1281", {"position": v(137.86, 65) * mm});
            skPoint(sketch, "E1282", {"position": v(131.51, 54) * mm});
            skLineSegment(sketch, "E1283", {"start": v(121.13, 66) * mm, "end": v(136.13, 66) * mm});
            skLineSegment(sketch, "E1284", {"start": v(121.13, 86) * mm, "end": v(136.13, 86) * mm});
            skLineSegment(sketch, "E1285", {"start": v(121.13, 86) * mm, "end": v(126.9, 76) * mm});
            skLineSegment(sketch, "E1286", {"start": v(126.9, 76) * mm, "end": v(121.13, 66) * mm});
            skLineSegment(sketch, "E1287", {"start": v(136.13, 86) * mm, "end": v(130.36, 76) * mm});
            skLineSegment(sketch, "E1288", {"start": v(130.36, 76) * mm, "end": v(136.13, 66) * mm});
            skPoint(sketch, "E1289", {"position": v(128.63, 87) * mm});
            skPoint(sketch, "E1289.positionSnap0", {"position": v(128.63, 86) * mm});
            skPoint(sketch, "E1290.positionSnap0", {"position": v(128.63, 66) * mm});
            skPoint(sketch, "E1291", {"position": v(122.57, 70.5) * mm});
            skPoint(sketch, "E1292", {"position": v(134.7, 70.5) * mm});
            skPoint(sketch, "E1293", {"position": v(134.79, 81.67) * mm});
            skPoint(sketch, "E1294", {"position": v(121.8, 82.85) * mm});
            skLineSegment(sketch, "E1295", {"start": v(131.51, 76) * mm, "end": v(131.17, 76.6) * mm});
            skPoint(sketch, "E1296", {"position": v(137.86, 87) * mm});
            skPoint(sketch, "E1297", {"position": v(131.51, 76) * mm});
            skLineSegment(sketch, "E1298", {"start": v(121.13, 88) * mm, "end": v(136.13, 88) * mm});
            skLineSegment(sketch, "E1299", {"start": v(121.13, 108) * mm, "end": v(136.13, 108) * mm});
            skLineSegment(sketch, "E1300", {"start": v(121.13, 108) * mm, "end": v(126.9, 98) * mm});
            skLineSegment(sketch, "E1301", {"start": v(126.9, 98) * mm, "end": v(121.13, 88) * mm});
            skLineSegment(sketch, "E1302", {"start": v(136.13, 108) * mm, "end": v(130.36, 98) * mm});
            skLineSegment(sketch, "E1303", {"start": v(130.36, 98) * mm, "end": v(136.13, 88) * mm});
            skPoint(sketch, "E1304", {"position": v(128.63, 109) * mm});
            skPoint(sketch, "E1304.positionSnap0", {"position": v(128.63, 108) * mm});
            skPoint(sketch, "E1305.positionSnap0", {"position": v(128.63, 88) * mm});
            skPoint(sketch, "E1306", {"position": v(122.57, 92.5) * mm});
            skPoint(sketch, "E1307", {"position": v(134.7, 92.5) * mm});
            skPoint(sketch, "E1308", {"position": v(134.79, 103.67) * mm});
            skPoint(sketch, "E1309", {"position": v(121.8, 104.85) * mm});
            skLineSegment(sketch, "E1310", {"start": v(131.51, 98) * mm, "end": v(131.17, 98.6) * mm});
            skPoint(sketch, "E1311", {"position": v(137.86, 109) * mm});
            skPoint(sketch, "E1312", {"position": v(131.51, 98) * mm});
            skLineSegment(sketch, "E1313", {"start": v(121.13, 110) * mm, "end": v(136.13, 110) * mm});
            skLineSegment(sketch, "E1314", {"start": v(121.13, 130) * mm, "end": v(136.13, 130) * mm});
            skLineSegment(sketch, "E1315", {"start": v(121.13, 130) * mm, "end": v(126.9, 120) * mm});
            skLineSegment(sketch, "E1316", {"start": v(126.9, 120) * mm, "end": v(121.13, 110) * mm});
            skLineSegment(sketch, "E1317", {"start": v(136.13, 130) * mm, "end": v(130.36, 120) * mm});
            skLineSegment(sketch, "E1318", {"start": v(130.36, 120) * mm, "end": v(136.13, 110) * mm});
            skPoint(sketch, "E1319", {"position": v(128.63, 131) * mm});
            skPoint(sketch, "E1319.positionSnap0", {"position": v(128.63, 130) * mm});
            skPoint(sketch, "E1320.positionSnap0", {"position": v(128.63, 110) * mm});
            skPoint(sketch, "E1321", {"position": v(122.57, 114.5) * mm});
            skPoint(sketch, "E1322", {"position": v(134.7, 114.5) * mm});
            skPoint(sketch, "E1323", {"position": v(134.79, 125.67) * mm});
            skPoint(sketch, "E1324", {"position": v(121.8, 126.85) * mm});
            skLineSegment(sketch, "E1325", {"start": v(131.51, 120) * mm, "end": v(131.17, 120.6) * mm});
            skPoint(sketch, "E1326", {"position": v(137.86, 131) * mm});
            skPoint(sketch, "E1327", {"position": v(131.51, 120) * mm});
            skLineSegment(sketch, "E1328", {"start": v(121.13, 132) * mm, "end": v(136.13, 132) * mm});
            skLineSegment(sketch, "E1329", {"start": v(121.13, 152) * mm, "end": v(136.13, 152) * mm});
            skLineSegment(sketch, "E1330", {"start": v(121.13, 152) * mm, "end": v(126.9, 142) * mm});
            skLineSegment(sketch, "E1331", {"start": v(126.9, 142) * mm, "end": v(121.13, 132) * mm});
            skLineSegment(sketch, "E1332", {"start": v(136.13, 152) * mm, "end": v(130.36, 142) * mm});
            skLineSegment(sketch, "E1333", {"start": v(130.36, 142) * mm, "end": v(136.13, 132) * mm});
            skPoint(sketch, "E1334", {"position": v(128.63, 153) * mm});
            skPoint(sketch, "E1334.positionSnap0", {"position": v(128.63, 152) * mm});
            skPoint(sketch, "E1335.positionSnap0", {"position": v(128.63, 132) * mm});
            skPoint(sketch, "E1336", {"position": v(122.57, 136.5) * mm});
            skPoint(sketch, "E1337", {"position": v(134.7, 136.5) * mm});
            skPoint(sketch, "E1338", {"position": v(134.79, 147.67) * mm});
            skPoint(sketch, "E1339", {"position": v(121.8, 148.85) * mm});
            skLineSegment(sketch, "E1340", {"start": v(131.51, 142) * mm, "end": v(131.17, 142.6) * mm});
            skPoint(sketch, "E1341", {"position": v(137.86, 153) * mm});
            skPoint(sketch, "E1342", {"position": v(131.51, 142) * mm});
            skLineSegment(sketch, "E1343", {"start": v(121.13, 154) * mm, "end": v(136.13, 154) * mm});
            skLineSegment(sketch, "E1344", {"start": v(121.13, 174) * mm, "end": v(136.13, 174) * mm});
            skLineSegment(sketch, "E1345", {"start": v(121.13, 174) * mm, "end": v(126.9, 164) * mm});
            skLineSegment(sketch, "E1346", {"start": v(126.9, 164) * mm, "end": v(121.13, 154) * mm});
            skLineSegment(sketch, "E1347", {"start": v(136.13, 174) * mm, "end": v(130.36, 164) * mm});
            skLineSegment(sketch, "E1348", {"start": v(130.36, 164) * mm, "end": v(136.13, 154) * mm});
            skPoint(sketch, "E1349", {"position": v(128.63, 175) * mm});
            skPoint(sketch, "E1349.positionSnap0", {"position": v(128.63, 174) * mm});
            skPoint(sketch, "E1350.positionSnap0", {"position": v(128.63, 154) * mm});
            skPoint(sketch, "E1351", {"position": v(122.57, 158.5) * mm});
            skPoint(sketch, "E1352", {"position": v(134.7, 158.5) * mm});
            skPoint(sketch, "E1353", {"position": v(134.79, 169.67) * mm});
            skPoint(sketch, "E1354", {"position": v(121.8, 170.85) * mm});
            skLineSegment(sketch, "E1355", {"start": v(131.51, 164) * mm, "end": v(131.17, 164.6) * mm});
            skPoint(sketch, "E1356", {"position": v(137.86, 175) * mm});
            skPoint(sketch, "E1357", {"position": v(131.51, 164) * mm});
            skLineSegment(sketch, "E1358", {"start": v(133.25, 11) * mm, "end": v(148.25, 11) * mm});
            skLineSegment(sketch, "E1359", {"start": v(133.25, 31) * mm, "end": v(148.25, 31) * mm});
            skLineSegment(sketch, "E1360", {"start": v(133.25, 31) * mm, "end": v(139.02, 21) * mm});
            skLineSegment(sketch, "E1361", {"start": v(139.02, 21) * mm, "end": v(133.25, 11) * mm});
            skLineSegment(sketch, "E1362", {"start": v(148.25, 31) * mm, "end": v(142.47, 21) * mm});
            skLineSegment(sketch, "E1363", {"start": v(142.47, 21) * mm, "end": v(148.25, 11) * mm});
            skPoint(sketch, "E1364", {"position": v(140.75, 32) * mm});
            skPoint(sketch, "E1364.positionSnap0", {"position": v(140.75, 31) * mm});
            skPoint(sketch, "E1365", {"position": v(140.75, 10) * mm});
            skPoint(sketch, "E1365.positionSnap0", {"position": v(140.75, 11) * mm});
            skPoint(sketch, "E1366", {"position": v(134.69, 15.5) * mm});
            skPoint(sketch, "E1367", {"position": v(146.8, 15.5) * mm});
            skPoint(sketch, "E1368", {"position": v(146.9, 26.67) * mm});
            skPoint(sketch, "E1369", {"position": v(133.91, 27.85) * mm});
            skLineSegment(sketch, "E1370", {"start": v(143.63, 21) * mm, "end": v(143.28, 21.6) * mm});
            skPoint(sketch, "E1371", {"position": v(149.98, 32) * mm});
            skPoint(sketch, "E1372", {"position": v(143.63, 21) * mm});
            skPoint(sketch, "E1373", {"position": v(149.98, 10) * mm});
            skLineSegment(sketch, "E1374", {"start": v(133.25, 33) * mm, "end": v(148.25, 33) * mm});
            skLineSegment(sketch, "E1375", {"start": v(133.25, 53) * mm, "end": v(148.25, 53) * mm});
            skLineSegment(sketch, "E1376", {"start": v(133.25, 53) * mm, "end": v(139.02, 43) * mm});
            skLineSegment(sketch, "E1377", {"start": v(139.02, 43) * mm, "end": v(133.25, 33) * mm});
            skLineSegment(sketch, "E1378", {"start": v(148.25, 53) * mm, "end": v(142.47, 43) * mm});
            skLineSegment(sketch, "E1379", {"start": v(142.47, 43) * mm, "end": v(148.25, 33) * mm});
            skPoint(sketch, "E1380", {"position": v(140.75, 54) * mm});
            skPoint(sketch, "E1380.positionSnap0", {"position": v(140.75, 53) * mm});
            skPoint(sketch, "E1381.positionSnap0", {"position": v(140.75, 33) * mm});
            skPoint(sketch, "E1382", {"position": v(134.69, 37.5) * mm});
            skPoint(sketch, "E1383", {"position": v(146.8, 37.5) * mm});
            skPoint(sketch, "E1384", {"position": v(146.9, 48.67) * mm});
            skPoint(sketch, "E1385", {"position": v(133.91, 49.85) * mm});
            skLineSegment(sketch, "E1386", {"start": v(143.63, 43) * mm, "end": v(143.28, 43.6) * mm});
            skPoint(sketch, "E1387", {"position": v(149.98, 54) * mm});
            skPoint(sketch, "E1388", {"position": v(143.63, 43) * mm});
            skLineSegment(sketch, "E1389", {"start": v(133.25, 55) * mm, "end": v(148.25, 55) * mm});
            skLineSegment(sketch, "E1390", {"start": v(133.25, 75) * mm, "end": v(148.25, 75) * mm});
            skLineSegment(sketch, "E1391", {"start": v(133.25, 75) * mm, "end": v(139.02, 65) * mm});
            skLineSegment(sketch, "E1392", {"start": v(139.02, 65) * mm, "end": v(133.25, 55) * mm});
            skLineSegment(sketch, "E1393", {"start": v(148.25, 75) * mm, "end": v(142.47, 65) * mm});
            skLineSegment(sketch, "E1394", {"start": v(142.47, 65) * mm, "end": v(148.25, 55) * mm});
            skPoint(sketch, "E1395", {"position": v(140.75, 76) * mm});
            skPoint(sketch, "E1395.positionSnap0", {"position": v(140.75, 75) * mm});
            skPoint(sketch, "E1396.positionSnap0", {"position": v(140.75, 55) * mm});
            skPoint(sketch, "E1397", {"position": v(134.69, 59.5) * mm});
            skPoint(sketch, "E1398", {"position": v(146.8, 59.5) * mm});
            skPoint(sketch, "E1399", {"position": v(146.9, 70.67) * mm});
            skPoint(sketch, "E1400", {"position": v(133.91, 71.85) * mm});
            skLineSegment(sketch, "E1401", {"start": v(143.63, 65) * mm, "end": v(143.28, 65.6) * mm});
            skPoint(sketch, "E1402", {"position": v(149.98, 76) * mm});
            skPoint(sketch, "E1403", {"position": v(143.63, 65) * mm});
            skLineSegment(sketch, "E1404", {"start": v(133.25, 77) * mm, "end": v(148.25, 77) * mm});
            skLineSegment(sketch, "E1405", {"start": v(133.25, 97) * mm, "end": v(148.25, 97) * mm});
            skLineSegment(sketch, "E1406", {"start": v(133.25, 97) * mm, "end": v(139.02, 87) * mm});
            skLineSegment(sketch, "E1407", {"start": v(139.02, 87) * mm, "end": v(133.25, 77) * mm});
            skLineSegment(sketch, "E1408", {"start": v(148.25, 97) * mm, "end": v(142.47, 87) * mm});
            skLineSegment(sketch, "E1409", {"start": v(142.47, 87) * mm, "end": v(148.25, 77) * mm});
            skPoint(sketch, "E1410", {"position": v(140.75, 98) * mm});
            skPoint(sketch, "E1410.positionSnap0", {"position": v(140.75, 97) * mm});
            skPoint(sketch, "E1411.positionSnap0", {"position": v(140.75, 77) * mm});
            skPoint(sketch, "E1412", {"position": v(134.69, 81.5) * mm});
            skPoint(sketch, "E1413", {"position": v(146.8, 81.5) * mm});
            skPoint(sketch, "E1414", {"position": v(146.9, 92.67) * mm});
            skPoint(sketch, "E1415", {"position": v(133.91, 93.85) * mm});
            skLineSegment(sketch, "E1416", {"start": v(143.63, 87) * mm, "end": v(143.28, 87.6) * mm});
            skPoint(sketch, "E1417", {"position": v(149.98, 98) * mm});
            skPoint(sketch, "E1418", {"position": v(143.63, 87) * mm});
            skLineSegment(sketch, "E1419", {"start": v(133.25, 99) * mm, "end": v(148.25, 99) * mm});
            skLineSegment(sketch, "E1420", {"start": v(133.25, 119) * mm, "end": v(148.25, 119) * mm});
            skLineSegment(sketch, "E1421", {"start": v(133.25, 119) * mm, "end": v(139.02, 109) * mm});
            skLineSegment(sketch, "E1422", {"start": v(139.02, 109) * mm, "end": v(133.25, 99) * mm});
            skLineSegment(sketch, "E1423", {"start": v(148.25, 119) * mm, "end": v(142.47, 109) * mm});
            skLineSegment(sketch, "E1424", {"start": v(142.47, 109) * mm, "end": v(148.25, 99) * mm});
            skPoint(sketch, "E1425", {"position": v(140.75, 120) * mm});
            skPoint(sketch, "E1425.positionSnap0", {"position": v(140.75, 119) * mm});
            skPoint(sketch, "E1426.positionSnap0", {"position": v(140.75, 99) * mm});
            skPoint(sketch, "E1427", {"position": v(134.69, 103.5) * mm});
            skPoint(sketch, "E1428", {"position": v(146.8, 103.5) * mm});
            skPoint(sketch, "E1429", {"position": v(146.9, 114.67) * mm});
            skPoint(sketch, "E1430", {"position": v(133.91, 115.85) * mm});
            skLineSegment(sketch, "E1431", {"start": v(143.63, 109) * mm, "end": v(143.28, 109.6) * mm});
            skPoint(sketch, "E1432", {"position": v(149.98, 120) * mm});
            skPoint(sketch, "E1433", {"position": v(143.63, 109) * mm});
            skLineSegment(sketch, "E1434", {"start": v(133.25, 121) * mm, "end": v(148.25, 121) * mm});
            skLineSegment(sketch, "E1435", {"start": v(133.25, 141) * mm, "end": v(148.25, 141) * mm});
            skLineSegment(sketch, "E1436", {"start": v(133.25, 141) * mm, "end": v(139.02, 131) * mm});
            skLineSegment(sketch, "E1437", {"start": v(139.02, 131) * mm, "end": v(133.25, 121) * mm});
            skLineSegment(sketch, "E1438", {"start": v(148.25, 141) * mm, "end": v(142.47, 131) * mm});
            skLineSegment(sketch, "E1439", {"start": v(142.47, 131) * mm, "end": v(148.25, 121) * mm});
            skPoint(sketch, "E1440", {"position": v(140.75, 142) * mm});
            skPoint(sketch, "E1440.positionSnap0", {"position": v(140.75, 141) * mm});
            skPoint(sketch, "E1441.positionSnap0", {"position": v(140.75, 121) * mm});
            skPoint(sketch, "E1442", {"position": v(134.69, 125.5) * mm});
            skPoint(sketch, "E1443", {"position": v(146.8, 125.5) * mm});
            skPoint(sketch, "E1444", {"position": v(146.9, 136.67) * mm});
            skPoint(sketch, "E1445", {"position": v(133.91, 137.85) * mm});
            skLineSegment(sketch, "E1446", {"start": v(143.63, 131) * mm, "end": v(143.28, 131.6) * mm});
            skPoint(sketch, "E1447", {"position": v(149.98, 142) * mm});
            skPoint(sketch, "E1448", {"position": v(143.63, 131) * mm});
            skLineSegment(sketch, "E1449", {"start": v(133.25, 143) * mm, "end": v(148.25, 143) * mm});
            skLineSegment(sketch, "E1450", {"start": v(133.25, 163) * mm, "end": v(148.25, 163) * mm});
            skLineSegment(sketch, "E1451", {"start": v(133.25, 163) * mm, "end": v(139.02, 153) * mm});
            skLineSegment(sketch, "E1452", {"start": v(139.02, 153) * mm, "end": v(133.25, 143) * mm});
            skLineSegment(sketch, "E1453", {"start": v(148.25, 163) * mm, "end": v(142.47, 153) * mm});
            skLineSegment(sketch, "E1454", {"start": v(142.47, 153) * mm, "end": v(148.25, 143) * mm});
            skPoint(sketch, "E1455", {"position": v(140.75, 164) * mm});
            skPoint(sketch, "E1455.positionSnap0", {"position": v(140.75, 163) * mm});
            skPoint(sketch, "E1456.positionSnap0", {"position": v(140.75, 143) * mm});
            skPoint(sketch, "E1457", {"position": v(134.69, 147.5) * mm});
            skPoint(sketch, "E1458", {"position": v(146.8, 147.5) * mm});
            skPoint(sketch, "E1459", {"position": v(146.9, 158.67) * mm});
            skPoint(sketch, "E1460", {"position": v(133.91, 159.85) * mm});
            skLineSegment(sketch, "E1461", {"start": v(143.63, 153) * mm, "end": v(143.28, 153.6) * mm});
            skPoint(sketch, "E1462", {"position": v(149.98, 164) * mm});
            skPoint(sketch, "E1463", {"position": v(143.63, 153) * mm});
            skLineSegment(sketch, "E1464", {"start": v(133.25, 165) * mm, "end": v(148.25, 165) * mm});
            skLineSegment(sketch, "E1465", {"start": v(133.25, 185) * mm, "end": v(148.25, 185) * mm});
            skLineSegment(sketch, "E1466", {"start": v(133.25, 185) * mm, "end": v(139.02, 175) * mm});
            skLineSegment(sketch, "E1467", {"start": v(139.02, 175) * mm, "end": v(133.25, 165) * mm});
            skLineSegment(sketch, "E1468", {"start": v(148.25, 185) * mm, "end": v(142.47, 175) * mm});
            skLineSegment(sketch, "E1469", {"start": v(142.47, 175) * mm, "end": v(148.25, 165) * mm});
            skPoint(sketch, "E1470", {"position": v(140.75, 186) * mm});
            skPoint(sketch, "E1470.positionSnap0", {"position": v(140.75, 185) * mm});
            skPoint(sketch, "E1471.positionSnap0", {"position": v(140.75, 165) * mm});
            skPoint(sketch, "E1472", {"position": v(134.69, 169.5) * mm});
            skPoint(sketch, "E1473", {"position": v(146.8, 169.5) * mm});
            skPoint(sketch, "E1474", {"position": v(146.9, 180.67) * mm});
            skPoint(sketch, "E1475", {"position": v(133.91, 181.85) * mm});
            skLineSegment(sketch, "E1476", {"start": v(143.63, 175) * mm, "end": v(143.28, 175.6) * mm});
            skPoint(sketch, "E1477", {"position": v(131.51, 186) * mm});
            skPoint(sketch, "E1478", {"position": v(149.98, 186) * mm});
            skPoint(sketch, "E1479", {"position": v(143.63, 175) * mm});
            skLineSegment(sketch, "E1480.bottom", {"start": v(-36.43, 201.1) * mm, "end": v(176.03, 201.1) * mm});
            skLineSegment(sketch, "E1480.top", {"start": v(-36.43, -13.62) * mm, "end": v(176.03, -13.62) * mm});
            skLineSegment(sketch, "E1480.left", {"start": v(-36.43, 201.1) * mm, "end": v(-36.43, -13.62) * mm});
            skLineSegment(sketch, "E1480.right", {"start": v(176.03, 201.1) * mm, "end": v(176.03, -13.62) * mm});
            skSolve(sketch);
        }
        {
            var Q0;
            Q0=qSketchRegion(id+"F0",true);
            extrude(context, id + "F1", {"entities" : qUnion([Q0]), "depth" : 50 * mm, "offsetDistance" : 25 * mm});
        }
    });
